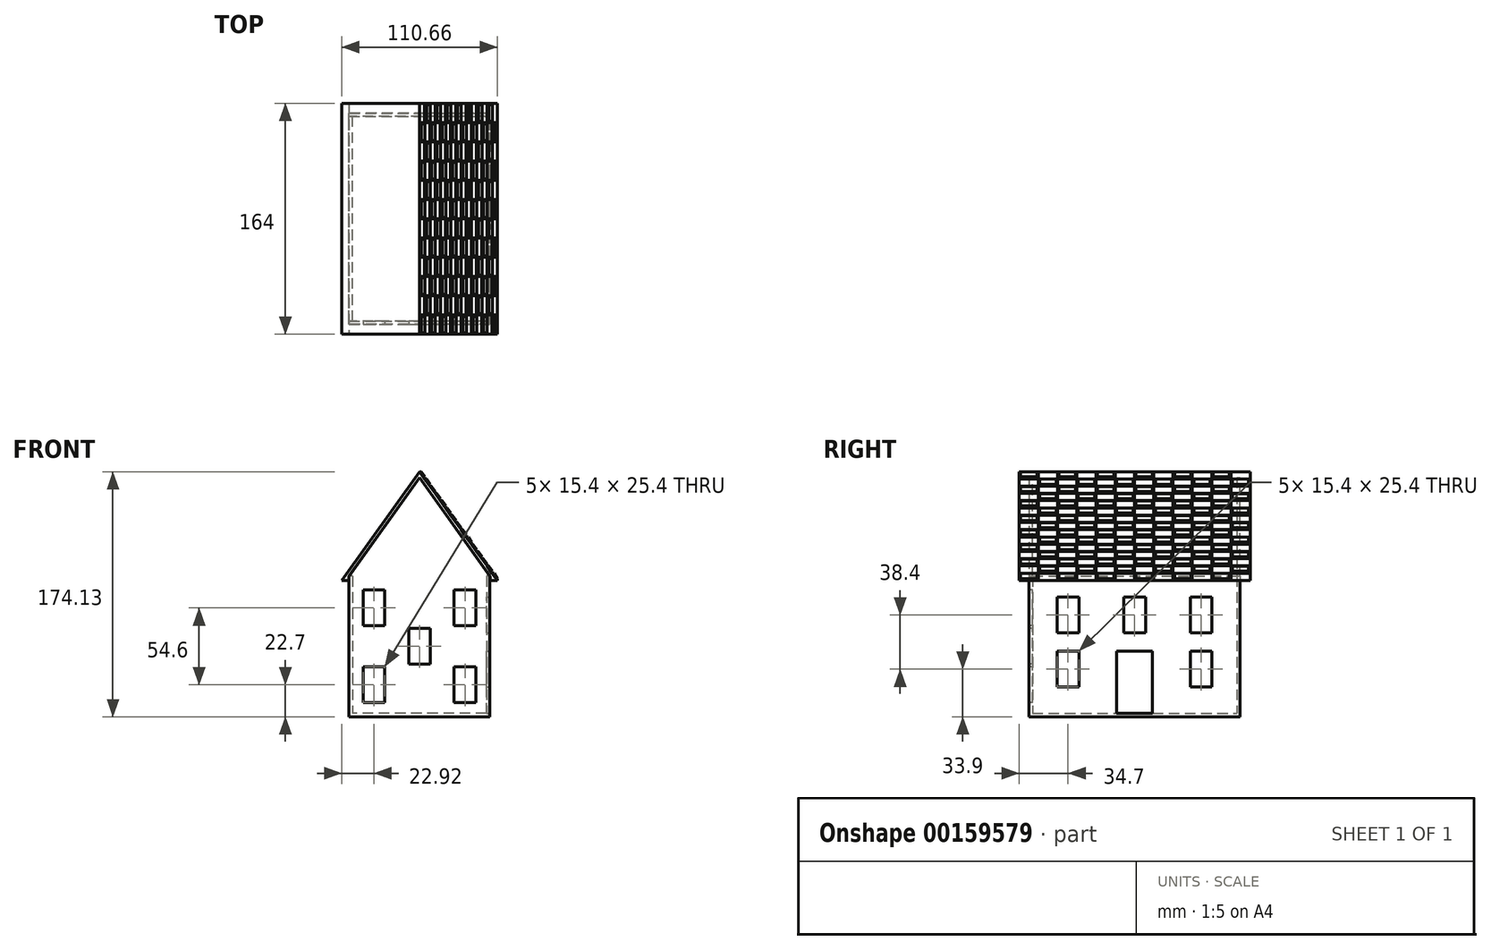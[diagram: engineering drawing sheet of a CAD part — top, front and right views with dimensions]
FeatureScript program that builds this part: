
annotation { "Feature Type Name" : "Feature", "Feature Type Description" : "" }
export const myFeature = defineFeature(function(context is Context, id is Id, definition is map)
    precondition{}
    {
        {
            assignVariable(context, id + "F0", {"name" : "T", "anyValue" : 2.4 * mm});
        }
        {
            var Q0;
            Q0=qCreatedBy(makeId("Top.planeOp"),FACE);
            var sketch = newSketch(context, id + "F1", { "sketchPlane" : qUnion([Q0])});
            skLineSegment(sketch, "E0.bottom", {"start": v(50, -75) * mm, "end": v(-50, -75) * mm});
            skLineSegment(sketch, "E0.top", {"start": v(50, 75) * mm, "end": v(-50, 75) * mm});
            skLineSegment(sketch, "E0.left", {"start": v(50, -75) * mm, "end": v(50, 75) * mm});
            skLineSegment(sketch, "E0.right", {"start": v(-50, -75) * mm, "end": v(-50, 75) * mm});
            skPoint(sketch, "E0.middle", {"position": v(0, 0) * mm});
            skSolve(sketch);
        }
        {
            var Q0;
            Q0=makeQuery(id+"F1.imprint","IMPRINT",FACE,{"disambiguationData":[TD([[makeQuery(id+"F1.imprint","IMPRINT",EDGE,{"derivedFrom":sQuery(id+"F1.wireOp",EDGE,"E0.bottom")}),-1.0]])]});
            extrude(context, id + "F2", {"entities" : qUnion([Q0]), "depth" : 100 * mm});
        }
        {
            var Q0;
            Q0=makeQuery(id+"F2.opExtrude","CAP_FACE",FACE,{"disambiguationData":[OSD([sQuery(id+"F1.wireOp",EDGE,"E0.bottom"),sQuery(id+"F1.wireOp",EDGE,"E0.top"),sQuery(id+"F1.wireOp",EDGE,"E0.left"),sQuery(id+"F1.wireOp",EDGE,"E0.right")])],"isStart":false});
            shell(context, id + "F3", {"entities" : qUnion([Q0]), "thickness" : getVariable(context, 'T')});
        }
        {
            var Q0;
            Q0=makeQuery(id+"F2.opExtrude","SWEPT_FACE",FACE,{"disambiguationData":[OSD([sQuery(id+"F1.wireOp",EDGE,"E0.bottom")])]});
            var sketch = newSketch(context, id + "F4", { "sketchPlane" : qUnion([Q0])});
            skLineSegment(sketch, "E1", {"start": v(-50, 100) * mm, "end": v(0, 170) * mm});
            skLineSegment(sketch, "E2", {"start": v(0, 170) * mm, "end": v(50, 100) * mm});
            skLineSegment(sketch, "E3", {"start": v(-50, 100) * mm, "end": v(50, 100) * mm});
            skSolve(sketch);
        }
        {
            var Q0;
            Q0=qSketchRegion(id+"F4",true);
            extrude(context, id + "F5", {"entities" : qUnion([Q0]), "operationType" : NewBodyOperationType.ADD, "oppositeDirection" : true, "depth" : getVariable(context, 'T')});
        }
        {
            var Q0;
            Q0=makeQuery(id+"F2.opExtrude","SWEPT_FACE",FACE,{"disambiguationData":[OSD([sQuery(id+"F1.wireOp",EDGE,"E0.top")])]});
            var sketch = newSketch(context, id + "F6", { "sketchPlane" : qUnion([Q0])});
            skLineSegment(sketch, "E4.0", {"start": v(50, 100) * mm, "end": v(-50, 100) * mm});
            skLineSegment(sketch, "E5.0", {"start": v(0, 170) * mm, "end": v(-50, 100) * mm});
            skLineSegment(sketch, "E6.0", {"start": v(50, 100) * mm, "end": v(0, 170) * mm});
            skSolve(sketch);
        }
        {
            var Q0;
            Q0=qSketchRegion(id+"F6",true);
            extrude(context, id + "F7", {"entities" : qUnion([Q0]), "operationType" : NewBodyOperationType.ADD, "oppositeDirection" : true, "depth" : getVariable(context, 'T')});
        }
        {
            var Q0;
            Q0=makeQuery(id+"F5.boolean.opBoolean","MERGE",FACE,{"derivedFrom":[makeQuery(id+"F2.opExtrude","SWEPT_FACE",FACE,{"disambiguationData":[OSD([sQuery(id+"F1.wireOp",EDGE,"E0.bottom")])]}),makeQuery(id+"F5.opExtrude","CAP_FACE",FACE,{"disambiguationData":[OSD([sQuery(id+"F4.wireOp",EDGE,"E1"),sQuery(id+"F4.wireOp",EDGE,"E2"),sQuery(id+"F4.wireOp",EDGE,"E3")])],"isStart":true})]});
            var sketch = newSketch(context, id + "F8", { "sketchPlane" : qUnion([Q0])});
            skLineSegment(sketch, "E7.bottom", {"start": v(-40, 90) * mm, "end": v(-24.6, 90) * mm});
            skLineSegment(sketch, "E7.top", {"start": v(-40, 64.6) * mm, "end": v(-24.6, 64.6) * mm});
            skLineSegment(sketch, "E7.left", {"start": v(-40, 90) * mm, "end": v(-40, 64.6) * mm});
            skLineSegment(sketch, "E7.right", {"start": v(-24.6, 90) * mm, "end": v(-24.6, 64.6) * mm});
            skLineSegment(sketch, "E8.bottom", {"start": v(24.6, 90) * mm, "end": v(40, 90) * mm});
            skLineSegment(sketch, "E8.top", {"start": v(24.6, 64.6) * mm, "end": v(40, 64.6) * mm});
            skLineSegment(sketch, "E8.left", {"start": v(24.6, 90) * mm, "end": v(24.6, 64.6) * mm});
            skLineSegment(sketch, "E8.right", {"start": v(40, 90) * mm, "end": v(40, 64.6) * mm});
            skPoint(sketch, "E9", {"position": v(0, 50) * mm});
            skLineSegment(sketch, "E10.bottom", {"start": v(-7.7, 62.7) * mm, "end": v(7.7, 62.7) * mm});
            skLineSegment(sketch, "E10.top", {"start": v(-7.7, 37.3) * mm, "end": v(7.7, 37.3) * mm});
            skLineSegment(sketch, "E10.left", {"start": v(-7.7, 62.7) * mm, "end": v(-7.7, 37.3) * mm});
            skLineSegment(sketch, "E10.right", {"start": v(7.7, 62.7) * mm, "end": v(7.7, 37.3) * mm});
            skLineSegment(sketch, "E11.bottom", {"start": v(-40, 35.4) * mm, "end": v(-24.6, 35.4) * mm});
            skLineSegment(sketch, "E11.top", {"start": v(-40, 10) * mm, "end": v(-24.6, 10) * mm});
            skLineSegment(sketch, "E11.left", {"start": v(-40, 35.4) * mm, "end": v(-40, 10) * mm});
            skLineSegment(sketch, "E11.right", {"start": v(-24.6, 35.4) * mm, "end": v(-24.6, 10) * mm});
            skLineSegment(sketch, "E12.bottom", {"start": v(24.6, 35.4) * mm, "end": v(40, 35.4) * mm});
            skLineSegment(sketch, "E12.top", {"start": v(24.6, 10) * mm, "end": v(40, 10) * mm});
            skLineSegment(sketch, "E12.left", {"start": v(24.6, 35.4) * mm, "end": v(24.6, 10) * mm});
            skLineSegment(sketch, "E12.right", {"start": v(40, 35.4) * mm, "end": v(40, 10) * mm});
            skPoint(sketch, "E13.positionSnap0", {"position": v(0, 62.7) * mm});
            skLineSegment(sketch, "E14", {"start": v(-66.45, 100) * mm, "end": v(66.45, 100) * mm, "construction": true});
            skLineSegment(sketch, "E15", {"start": v(-66.45, 90) * mm, "end": v(66.45, 90) * mm, "construction": true});
            skLineSegment(sketch, "E16", {"start": v(-66.45, 0) * mm, "end": v(66.45, 0) * mm, "construction": true});
            skLineSegment(sketch, "E17", {"start": v(-50, 110.2) * mm, "end": v(-50, -10.46) * mm, "construction": true});
            skLineSegment(sketch, "E18", {"start": v(-40, 110.2) * mm, "end": v(-40, -10.46) * mm, "construction": true});
            skLineSegment(sketch, "E19", {"start": v(50, 110.2) * mm, "end": v(50, -10.46) * mm, "construction": true});
            skLineSegment(sketch, "E20", {"start": v(40, 110.2) * mm, "end": v(40, -10.46) * mm, "construction": true});
            skPoint(sketch, "E21", {"position": v(-40, 49.87) * mm});
            skPoint(sketch, "E22", {"position": v(-50, 50) * mm});
            skPoint(sketch, "E23", {"position": v(0, 90) * mm});
            skLineSegment(sketch, "E24", {"start": v(66.45, 10) * mm, "end": v(-66.45, 10) * mm, "construction": true});
            skSolve(sketch);
        }
        {
            var Q0;
            Q0=makeQuery(id+"F8.imprint","IMPRINT",FACE,{"disambiguationData":[TD([[makeQuery(id+"F8.imprint","IMPRINT",EDGE,{"derivedFrom":sQuery(id+"F8.wireOp",EDGE,"E7.bottom")}),-1.0]])]});
            var Q1;
            Q1=makeQuery(id+"F8.imprint","IMPRINT",FACE,{"disambiguationData":[TD([[makeQuery(id+"F8.imprint","IMPRINT",EDGE,{"derivedFrom":sQuery(id+"F8.wireOp",EDGE,"E8.bottom")}),-1.0]])]});
            var Q2;
            Q2=makeQuery(id+"F8.imprint","IMPRINT",FACE,{"disambiguationData":[TD([[makeQuery(id+"F8.imprint","IMPRINT",EDGE,{"derivedFrom":sQuery(id+"F8.wireOp",EDGE,"E10.bottom")}),-1.0]])]});
            var Q3;
            Q3=makeQuery(id+"F8.imprint","IMPRINT",FACE,{"disambiguationData":[TD([[makeQuery(id+"F8.imprint","IMPRINT",EDGE,{"derivedFrom":sQuery(id+"F8.wireOp",EDGE,"E12.bottom")}),-1.0]])]});
            var Q4;
            Q4=makeQuery(id+"F8.imprint","IMPRINT",FACE,{"disambiguationData":[TD([[makeQuery(id+"F8.imprint","IMPRINT",EDGE,{"derivedFrom":sQuery(id+"F8.wireOp",EDGE,"E11.bottom")}),-1.0]])]});
            extrude(context, id + "F9", {"entities" : qUnion([Q0, Q1, Q2, Q3, Q4]), "operationType" : NewBodyOperationType.REMOVE, "endBound" : BoundingType.UP_TO_NEXT, "oppositeDirection" : true, "depth" : 25 * mm});
        }
        {
            var Q0;
            Q0=makeQuery(id+"F2.opExtrude","SWEPT_FACE",FACE,{"disambiguationData":[OSD([sQuery(id+"F1.wireOp",EDGE,"E0.left")])]});
            var sketch = newSketch(context, id + "F10", { "sketchPlane" : qUnion([Q0])});
            skLineSegment(sketch, "E25.bottom", {"start": v(-39.6, 59.6) * mm, "end": v(-55, 59.6) * mm});
            skLineSegment(sketch, "E25.top", {"start": v(-39.6, 85) * mm, "end": v(-55, 85) * mm});
            skLineSegment(sketch, "E25.left", {"start": v(-39.6, 59.6) * mm, "end": v(-39.6, 85) * mm});
            skLineSegment(sketch, "E25.right", {"start": v(-55, 59.6) * mm, "end": v(-55, 85) * mm});
            skPoint(sketch, "E25.middle", {"position": v(-47.3, 72.3) * mm});
            skLineSegment(sketch, "E26.bottom", {"start": v(55, 59.6) * mm, "end": v(39.6, 59.6) * mm});
            skLineSegment(sketch, "E26.top", {"start": v(55, 85) * mm, "end": v(39.6, 85) * mm});
            skLineSegment(sketch, "E26.left", {"start": v(55, 59.6) * mm, "end": v(55, 85) * mm});
            skLineSegment(sketch, "E26.right", {"start": v(39.6, 59.6) * mm, "end": v(39.6, 85) * mm});
            skPoint(sketch, "E26.middle", {"position": v(47.3, 72.3) * mm});
            skLineSegment(sketch, "E27.bottom", {"start": v(-39.6, 21.2) * mm, "end": v(-55, 21.2) * mm});
            skLineSegment(sketch, "E27.top", {"start": v(-39.6, 46.6) * mm, "end": v(-55, 46.6) * mm});
            skLineSegment(sketch, "E27.left", {"start": v(-39.6, 21.2) * mm, "end": v(-39.6, 46.6) * mm});
            skLineSegment(sketch, "E27.right", {"start": v(-55, 21.2) * mm, "end": v(-55, 46.6) * mm});
            skPoint(sketch, "E27.middle", {"position": v(-47.3, 33.9) * mm});
            skLineSegment(sketch, "E28.bottom", {"start": v(55, 21.2) * mm, "end": v(39.6, 21.2) * mm});
            skLineSegment(sketch, "E28.top", {"start": v(55, 46.6) * mm, "end": v(39.6, 46.6) * mm});
            skLineSegment(sketch, "E28.left", {"start": v(55, 21.2) * mm, "end": v(55, 46.6) * mm});
            skLineSegment(sketch, "E28.right", {"start": v(39.6, 21.2) * mm, "end": v(39.6, 46.6) * mm});
            skPoint(sketch, "E28.middle", {"position": v(47.3, 33.9) * mm});
            skLineSegment(sketch, "E29.bottom", {"start": v(7.7, 59.6) * mm, "end": v(-7.7, 59.6) * mm});
            skLineSegment(sketch, "E29.top", {"start": v(7.7, 85) * mm, "end": v(-7.7, 85) * mm});
            skLineSegment(sketch, "E29.left", {"start": v(7.7, 59.6) * mm, "end": v(7.7, 85) * mm});
            skLineSegment(sketch, "E29.right", {"start": v(-7.7, 59.6) * mm, "end": v(-7.7, 85) * mm});
            skPoint(sketch, "E29.middle", {"position": v(0, 72.3) * mm});
            skLineSegment(sketch, "E30", {"start": v(-82.85, 2.4) * mm, "end": v(78.68, 2.4) * mm, "construction": true});
            skLineSegment(sketch, "E31.bottom", {"start": v(-12.7, 2.4) * mm, "end": v(12.7, 2.4) * mm});
            skLineSegment(sketch, "E31.top", {"start": v(-12.7, 46.6) * mm, "end": v(12.7, 46.6) * mm});
            skLineSegment(sketch, "E31.left", {"start": v(-12.7, 2.4) * mm, "end": v(-12.7, 46.6) * mm});
            skLineSegment(sketch, "E31.right", {"start": v(12.7, 2.4) * mm, "end": v(12.7, 46.6) * mm});
            skPoint(sketch, "E32", {"position": v(0, 46.6) * mm});
            skSolve(sketch);
        }
        {
            var Q0;
            Q0=qSketchRegion(id+"F10",true);
            extrude(context, id + "F11", {"entities" : qUnion([Q0]), "operationType" : NewBodyOperationType.REMOVE, "endBound" : BoundingType.UP_TO_NEXT, "oppositeDirection" : true, "depth" : 25 * mm});
        }
        {
            var Q0;
            Q0=makeQuery(id+"F5.boolean.opBoolean","MERGE",FACE,{"derivedFrom":[makeQuery(id+"F2.opExtrude","SWEPT_FACE",FACE,{"disambiguationData":[OSD([sQuery(id+"F1.wireOp",EDGE,"E0.bottom")])]}),makeQuery(id+"F5.opExtrude","CAP_FACE",FACE,{"disambiguationData":[OSD([sQuery(id+"F4.wireOp",EDGE,"E1"),sQuery(id+"F4.wireOp",EDGE,"E2"),sQuery(id+"F4.wireOp",EDGE,"E3")])],"isStart":true})]});
            cPlane(context, id + "F12", {"entities" : qUnion([Q0]), "cplaneType" : CPlaneType.OFFSET, "offset" : 7 * mm, "width" : 150 * mm, "height" : 150 * mm});
        }
        {
            var Q0;
            Q0=makeQuery(id+"F7.boolean.opBoolean","MERGE",FACE,{"derivedFrom":[makeQuery(id+"F2.opExtrude","SWEPT_FACE",FACE,{"disambiguationData":[OSD([sQuery(id+"F1.wireOp",EDGE,"E0.top")])]}),makeQuery(id+"F7.opExtrude","CAP_FACE",FACE,{"disambiguationData":[OSD([sQuery(id+"F6.wireOp",EDGE,"E4.0"),sQuery(id+"F6.wireOp",EDGE,"E5.0"),sQuery(id+"F6.wireOp",EDGE,"E6.0")])],"isStart":true})]});
            cPlane(context, id + "F13", {"entities" : qUnion([Q0]), "cplaneType" : CPlaneType.OFFSET, "offset" : 7 * mm, "width" : 150 * mm, "height" : 150 * mm});
        }
        {
            var Q0;
            Q0=qCreatedBy(id+"F12.planeOp",FACE);
            var sketch = newSketch(context, id + "F14", { "sketchPlane" : qUnion([Q0])});
            skPoint(sketch, "E33", {"position": v(0, 170) * mm});
            skPoint(sketch, "E34", {"position": v(50, 100) * mm});
            skPoint(sketch, "E35", {"position": v(-50, 100) * mm});
            skLineSegment(sketch, "E36", {"start": v(-55.22, 96.82) * mm, "end": v(0, 174.13) * mm});
            skLineSegment(sketch, "E37", {"start": v(-55.22, 96.82) * mm, "end": v(-50.2, 96.82) * mm});
            skLineSegment(sketch, "E38", {"start": v(0, 170) * mm, "end": v(-50, 100) * mm});
            skLineSegment(sketch, "E39", {"start": v(-50, 100) * mm, "end": v(-50.2, 99.72) * mm});
            skLineSegment(sketch, "E40", {"start": v(-50.2, 99.72) * mm, "end": v(-50.2, 96.82) * mm});
            skLineSegment(sketch, "E41", {"start": v(0, 181.99) * mm, "end": v(0, -15.78) * mm, "construction": true});
            skLineSegment(sketch, "E42.MirrorCS", {"start": v(0, 170) * mm, "end": v(50, 100) * mm});
            skLineSegment(sketch, "E43.MirrorCS", {"start": v(50, 100) * mm, "end": v(50.2, 99.72) * mm});
            skLineSegment(sketch, "E44.MirrorCS", {"start": v(50.2, 99.72) * mm, "end": v(50.2, 96.82) * mm});
            skLineSegment(sketch, "E45.MirrorCS", {"start": v(55.22, 96.82) * mm, "end": v(0, 174.13) * mm});
            skLineSegment(sketch, "E46.MirrorCS", {"start": v(55.22, 96.82) * mm, "end": v(50.2, 96.82) * mm});
            skSolve(sketch);
        }
        {
            var Q0;
            Q0=qSketchRegion(id+"F14",true);
            var Q1;
            Q1=qCreatedBy(id+"F13.planeOp",FACE);
            extrude(context, id + "F15", {"entities" : qUnion([Q0]), "oppositeDirection" : true, "endBoundEntityFace" : qUnion([Q1]), "depth" : 164 * mm});
        }
        {
            var Q0;
            Q0=makeQuery(id+"F15.opExtrude","SWEPT_FACE",FACE,{"disambiguationData":[OSD([sQuery(id+"F14.wireOp",EDGE,"E45.MirrorCS")])]});
            var sketch = newSketch(context, id + "F16", { "sketchPlane" : qUnion([Q0])});
            skLineSegment(sketch, "E47", {"start": v(-82, 141.7) * mm, "end": v(-68.33, 141.7) * mm});
            skLineSegment(sketch, "E48", {"start": v(-68.33, 141.7) * mm, "end": v(-68.33, 135.36) * mm});
            skLineSegment(sketch, "E49", {"start": v(-68.33, 135.36) * mm, "end": v(-82, 135.36) * mm});
            skLineSegment(sketch, "E50", {"start": v(-82, 135.36) * mm, "end": v(-82, 141.7) * mm});
            skLineSegment(sketch, "E51.0.1.0", {"start": v(-82, 129.03) * mm, "end": v(-68.33, 129.03) * mm});
            skLineSegment(sketch, "E51.0.1.1", {"start": v(-82, 122.7) * mm, "end": v(-82, 129.03) * mm});
            skLineSegment(sketch, "E51.0.1.2", {"start": v(-68.33, 129.03) * mm, "end": v(-68.33, 122.7) * mm});
            skLineSegment(sketch, "E51.0.1.3", {"start": v(-68.33, 122.7) * mm, "end": v(-82, 122.7) * mm});
            skLineSegment(sketch, "E51.0.2.0", {"start": v(-82, 116.37) * mm, "end": v(-68.33, 116.37) * mm});
            skLineSegment(sketch, "E51.0.2.1", {"start": v(-82, 110.03) * mm, "end": v(-82, 116.37) * mm});
            skLineSegment(sketch, "E51.0.2.2", {"start": v(-68.33, 116.37) * mm, "end": v(-68.33, 110.03) * mm});
            skLineSegment(sketch, "E51.0.2.3", {"start": v(-68.33, 110.03) * mm, "end": v(-82, 110.03) * mm});
            skLineSegment(sketch, "E51.0.3.0", {"start": v(-82, 103.7) * mm, "end": v(-68.33, 103.7) * mm});
            skLineSegment(sketch, "E51.0.3.1", {"start": v(-82, 97.37) * mm, "end": v(-82, 103.7) * mm});
            skLineSegment(sketch, "E51.0.3.2", {"start": v(-68.33, 103.7) * mm, "end": v(-68.33, 97.37) * mm});
            skLineSegment(sketch, "E51.0.3.3", {"start": v(-68.33, 97.37) * mm, "end": v(-82, 97.37) * mm});
            skLineSegment(sketch, "E51.0.4.0", {"start": v(-82, 91.04) * mm, "end": v(-68.33, 91.04) * mm});
            skLineSegment(sketch, "E51.0.4.1", {"start": v(-82, 84.7) * mm, "end": v(-82, 91.04) * mm});
            skLineSegment(sketch, "E51.0.4.2", {"start": v(-68.33, 91.04) * mm, "end": v(-68.33, 84.7) * mm});
            skLineSegment(sketch, "E51.0.4.3", {"start": v(-68.33, 84.7) * mm, "end": v(-82, 84.7) * mm});
            skLineSegment(sketch, "E51.0.5.0", {"start": v(-82, 78.38) * mm, "end": v(-68.33, 78.38) * mm});
            skLineSegment(sketch, "E51.0.5.1", {"start": v(-82, 72.04) * mm, "end": v(-82, 78.38) * mm});
            skLineSegment(sketch, "E51.0.5.2", {"start": v(-68.33, 78.38) * mm, "end": v(-68.33, 72.04) * mm});
            skLineSegment(sketch, "E51.0.5.3", {"start": v(-68.33, 72.04) * mm, "end": v(-82, 72.04) * mm});
            skLineSegment(sketch, "E51.0.6.0", {"start": v(-82, 65.71) * mm, "end": v(-68.33, 65.71) * mm});
            skLineSegment(sketch, "E51.0.6.1", {"start": v(-82, 59.38) * mm, "end": v(-82, 65.71) * mm});
            skLineSegment(sketch, "E51.0.6.2", {"start": v(-68.33, 65.71) * mm, "end": v(-68.33, 59.38) * mm});
            skLineSegment(sketch, "E51.0.6.3", {"start": v(-68.33, 59.38) * mm, "end": v(-82, 59.38) * mm});
            skLineSegment(sketch, "E51.0.7.0", {"start": v(-82, 53.05) * mm, "end": v(-68.33, 53.05) * mm});
            skLineSegment(sketch, "E51.0.7.1", {"start": v(-82, 46.72) * mm, "end": v(-82, 53.05) * mm});
            skLineSegment(sketch, "E51.0.7.2", {"start": v(-68.33, 53.05) * mm, "end": v(-68.33, 46.72) * mm});
            skLineSegment(sketch, "E51.0.7.3", {"start": v(-68.33, 46.72) * mm, "end": v(-82, 46.72) * mm});
            skLineSegment(sketch, "E51.1.0.0", {"start": v(-54.67, 141.7) * mm, "end": v(-41, 141.7) * mm});
            skLineSegment(sketch, "E51.1.0.1", {"start": v(-54.67, 135.36) * mm, "end": v(-54.67, 141.7) * mm});
            skLineSegment(sketch, "E51.1.0.2", {"start": v(-41, 141.7) * mm, "end": v(-41, 135.36) * mm});
            skLineSegment(sketch, "E51.1.0.3", {"start": v(-41, 135.36) * mm, "end": v(-54.67, 135.36) * mm});
            skLineSegment(sketch, "E51.1.1.0", {"start": v(-54.67, 129.03) * mm, "end": v(-41, 129.03) * mm});
            skLineSegment(sketch, "E51.1.1.1", {"start": v(-54.67, 122.7) * mm, "end": v(-54.67, 129.03) * mm});
            skLineSegment(sketch, "E51.1.1.2", {"start": v(-41, 129.03) * mm, "end": v(-41, 122.7) * mm});
            skLineSegment(sketch, "E51.1.1.3", {"start": v(-41, 122.7) * mm, "end": v(-54.67, 122.7) * mm});
            skLineSegment(sketch, "E51.1.2.0", {"start": v(-54.67, 116.37) * mm, "end": v(-41, 116.37) * mm});
            skLineSegment(sketch, "E51.1.2.1", {"start": v(-54.67, 110.03) * mm, "end": v(-54.67, 116.37) * mm});
            skLineSegment(sketch, "E51.1.2.2", {"start": v(-41, 116.37) * mm, "end": v(-41, 110.03) * mm});
            skLineSegment(sketch, "E51.1.2.3", {"start": v(-41, 110.03) * mm, "end": v(-54.67, 110.03) * mm});
            skLineSegment(sketch, "E51.1.3.0", {"start": v(-54.67, 103.7) * mm, "end": v(-41, 103.7) * mm});
            skLineSegment(sketch, "E51.1.3.1", {"start": v(-54.67, 97.37) * mm, "end": v(-54.67, 103.7) * mm});
            skLineSegment(sketch, "E51.1.3.2", {"start": v(-41, 103.7) * mm, "end": v(-41, 97.37) * mm});
            skLineSegment(sketch, "E51.1.3.3", {"start": v(-41, 97.37) * mm, "end": v(-54.67, 97.37) * mm});
            skLineSegment(sketch, "E51.1.4.0", {"start": v(-54.67, 91.04) * mm, "end": v(-41, 91.04) * mm});
            skLineSegment(sketch, "E51.1.4.1", {"start": v(-54.67, 84.7) * mm, "end": v(-54.67, 91.04) * mm});
            skLineSegment(sketch, "E51.1.4.2", {"start": v(-41, 91.04) * mm, "end": v(-41, 84.7) * mm});
            skLineSegment(sketch, "E51.1.4.3", {"start": v(-41, 84.7) * mm, "end": v(-54.67, 84.7) * mm});
            skLineSegment(sketch, "E51.1.5.0", {"start": v(-54.67, 78.38) * mm, "end": v(-41, 78.38) * mm});
            skLineSegment(sketch, "E51.1.5.1", {"start": v(-54.67, 72.04) * mm, "end": v(-54.67, 78.38) * mm});
            skLineSegment(sketch, "E51.1.5.2", {"start": v(-41, 78.38) * mm, "end": v(-41, 72.04) * mm});
            skLineSegment(sketch, "E51.1.5.3", {"start": v(-41, 72.04) * mm, "end": v(-54.67, 72.04) * mm});
            skLineSegment(sketch, "E51.1.6.0", {"start": v(-54.67, 65.71) * mm, "end": v(-41, 65.71) * mm});
            skLineSegment(sketch, "E51.1.6.1", {"start": v(-54.67, 59.38) * mm, "end": v(-54.67, 65.71) * mm});
            skLineSegment(sketch, "E51.1.6.2", {"start": v(-41, 65.71) * mm, "end": v(-41, 59.38) * mm});
            skLineSegment(sketch, "E51.1.6.3", {"start": v(-41, 59.38) * mm, "end": v(-54.67, 59.38) * mm});
            skLineSegment(sketch, "E51.1.7.0", {"start": v(-54.67, 53.05) * mm, "end": v(-41, 53.05) * mm});
            skLineSegment(sketch, "E51.1.7.1", {"start": v(-54.67, 46.72) * mm, "end": v(-54.67, 53.05) * mm});
            skLineSegment(sketch, "E51.1.7.2", {"start": v(-41, 53.05) * mm, "end": v(-41, 46.72) * mm});
            skLineSegment(sketch, "E51.1.7.3", {"start": v(-41, 46.72) * mm, "end": v(-54.67, 46.72) * mm});
            skLineSegment(sketch, "E51.2.0.0", {"start": v(-27.33, 141.7) * mm, "end": v(-13.67, 141.7) * mm});
            skLineSegment(sketch, "E51.2.0.1", {"start": v(-27.33, 135.36) * mm, "end": v(-27.33, 141.7) * mm});
            skLineSegment(sketch, "E51.2.0.2", {"start": v(-13.67, 141.7) * mm, "end": v(-13.67, 135.36) * mm});
            skLineSegment(sketch, "E51.2.0.3", {"start": v(-13.67, 135.36) * mm, "end": v(-27.33, 135.36) * mm});
            skLineSegment(sketch, "E51.2.1.0", {"start": v(-27.33, 129.03) * mm, "end": v(-13.67, 129.03) * mm});
            skLineSegment(sketch, "E51.2.1.1", {"start": v(-27.33, 122.7) * mm, "end": v(-27.33, 129.03) * mm});
            skLineSegment(sketch, "E51.2.1.2", {"start": v(-13.67, 129.03) * mm, "end": v(-13.67, 122.7) * mm});
            skLineSegment(sketch, "E51.2.1.3", {"start": v(-13.67, 122.7) * mm, "end": v(-27.33, 122.7) * mm});
            skLineSegment(sketch, "E51.2.2.0", {"start": v(-27.33, 116.37) * mm, "end": v(-13.67, 116.37) * mm});
            skLineSegment(sketch, "E51.2.2.1", {"start": v(-27.33, 110.03) * mm, "end": v(-27.33, 116.37) * mm});
            skLineSegment(sketch, "E51.2.2.2", {"start": v(-13.67, 116.37) * mm, "end": v(-13.67, 110.03) * mm});
            skLineSegment(sketch, "E51.2.2.3", {"start": v(-13.67, 110.03) * mm, "end": v(-27.33, 110.03) * mm});
            skLineSegment(sketch, "E51.2.3.0", {"start": v(-27.33, 103.7) * mm, "end": v(-13.67, 103.7) * mm});
            skLineSegment(sketch, "E51.2.3.1", {"start": v(-27.33, 97.37) * mm, "end": v(-27.33, 103.7) * mm});
            skLineSegment(sketch, "E51.2.3.2", {"start": v(-13.67, 103.7) * mm, "end": v(-13.67, 97.37) * mm});
            skLineSegment(sketch, "E51.2.3.3", {"start": v(-13.67, 97.37) * mm, "end": v(-27.33, 97.37) * mm});
            skLineSegment(sketch, "E51.2.4.0", {"start": v(-27.33, 91.04) * mm, "end": v(-13.67, 91.04) * mm});
            skLineSegment(sketch, "E51.2.4.1", {"start": v(-27.33, 84.7) * mm, "end": v(-27.33, 91.04) * mm});
            skLineSegment(sketch, "E51.2.4.2", {"start": v(-13.67, 91.04) * mm, "end": v(-13.67, 84.7) * mm});
            skLineSegment(sketch, "E51.2.4.3", {"start": v(-13.67, 84.7) * mm, "end": v(-27.33, 84.7) * mm});
            skLineSegment(sketch, "E51.2.5.0", {"start": v(-27.33, 78.38) * mm, "end": v(-13.67, 78.38) * mm});
            skLineSegment(sketch, "E51.2.5.1", {"start": v(-27.33, 72.04) * mm, "end": v(-27.33, 78.38) * mm});
            skLineSegment(sketch, "E51.2.5.2", {"start": v(-13.67, 78.38) * mm, "end": v(-13.67, 72.04) * mm});
            skLineSegment(sketch, "E51.2.5.3", {"start": v(-13.67, 72.04) * mm, "end": v(-27.33, 72.04) * mm});
            skLineSegment(sketch, "E51.2.6.0", {"start": v(-27.33, 65.71) * mm, "end": v(-13.67, 65.71) * mm});
            skLineSegment(sketch, "E51.2.6.1", {"start": v(-27.33, 59.38) * mm, "end": v(-27.33, 65.71) * mm});
            skLineSegment(sketch, "E51.2.6.2", {"start": v(-13.67, 65.71) * mm, "end": v(-13.67, 59.38) * mm});
            skLineSegment(sketch, "E51.2.6.3", {"start": v(-13.67, 59.38) * mm, "end": v(-27.33, 59.38) * mm});
            skLineSegment(sketch, "E51.2.7.0", {"start": v(-27.33, 53.05) * mm, "end": v(-13.67, 53.05) * mm});
            skLineSegment(sketch, "E51.2.7.1", {"start": v(-27.33, 46.72) * mm, "end": v(-27.33, 53.05) * mm});
            skLineSegment(sketch, "E51.2.7.2", {"start": v(-13.67, 53.05) * mm, "end": v(-13.67, 46.72) * mm});
            skLineSegment(sketch, "E51.2.7.3", {"start": v(-13.67, 46.72) * mm, "end": v(-27.33, 46.72) * mm});
            skLineSegment(sketch, "E51.3.0.0", {"start": v(0, 141.7) * mm, "end": v(13.67, 141.7) * mm});
            skLineSegment(sketch, "E51.3.0.1", {"start": v(0, 135.36) * mm, "end": v(0, 141.7) * mm});
            skLineSegment(sketch, "E51.3.0.2", {"start": v(13.67, 141.7) * mm, "end": v(13.67, 135.36) * mm});
            skLineSegment(sketch, "E51.3.0.3", {"start": v(13.67, 135.36) * mm, "end": v(0, 135.36) * mm});
            skLineSegment(sketch, "E51.3.1.0", {"start": v(0, 129.03) * mm, "end": v(13.67, 129.03) * mm});
            skLineSegment(sketch, "E51.3.1.1", {"start": v(0, 122.7) * mm, "end": v(0, 129.03) * mm});
            skLineSegment(sketch, "E51.3.1.2", {"start": v(13.67, 129.03) * mm, "end": v(13.67, 122.7) * mm});
            skLineSegment(sketch, "E51.3.1.3", {"start": v(13.67, 122.7) * mm, "end": v(0, 122.7) * mm});
            skLineSegment(sketch, "E51.3.2.0", {"start": v(0, 116.37) * mm, "end": v(13.67, 116.37) * mm});
            skLineSegment(sketch, "E51.3.2.1", {"start": v(0, 110.03) * mm, "end": v(0, 116.37) * mm});
            skLineSegment(sketch, "E51.3.2.2", {"start": v(13.67, 116.37) * mm, "end": v(13.67, 110.03) * mm});
            skLineSegment(sketch, "E51.3.2.3", {"start": v(13.67, 110.03) * mm, "end": v(0, 110.03) * mm});
            skLineSegment(sketch, "E51.3.3.0", {"start": v(0, 103.7) * mm, "end": v(13.67, 103.7) * mm});
            skLineSegment(sketch, "E51.3.3.1", {"start": v(0, 97.37) * mm, "end": v(0, 103.7) * mm});
            skLineSegment(sketch, "E51.3.3.2", {"start": v(13.67, 103.7) * mm, "end": v(13.67, 97.37) * mm});
            skLineSegment(sketch, "E51.3.3.3", {"start": v(13.67, 97.37) * mm, "end": v(0, 97.37) * mm});
            skLineSegment(sketch, "E51.3.4.0", {"start": v(0, 91.04) * mm, "end": v(13.67, 91.04) * mm});
            skLineSegment(sketch, "E51.3.4.1", {"start": v(0, 84.7) * mm, "end": v(0, 91.04) * mm});
            skLineSegment(sketch, "E51.3.4.2", {"start": v(13.67, 91.04) * mm, "end": v(13.67, 84.7) * mm});
            skLineSegment(sketch, "E51.3.4.3", {"start": v(13.67, 84.7) * mm, "end": v(0, 84.7) * mm});
            skLineSegment(sketch, "E51.3.5.0", {"start": v(0, 78.38) * mm, "end": v(13.67, 78.38) * mm});
            skLineSegment(sketch, "E51.3.5.1", {"start": v(0, 72.04) * mm, "end": v(0, 78.38) * mm});
            skLineSegment(sketch, "E51.3.5.2", {"start": v(13.67, 78.38) * mm, "end": v(13.67, 72.04) * mm});
            skLineSegment(sketch, "E51.3.5.3", {"start": v(13.67, 72.04) * mm, "end": v(0, 72.04) * mm});
            skLineSegment(sketch, "E51.3.6.0", {"start": v(0, 65.71) * mm, "end": v(13.67, 65.71) * mm});
            skLineSegment(sketch, "E51.3.6.1", {"start": v(0, 59.38) * mm, "end": v(0, 65.71) * mm});
            skLineSegment(sketch, "E51.3.6.2", {"start": v(13.67, 65.71) * mm, "end": v(13.67, 59.38) * mm});
            skLineSegment(sketch, "E51.3.6.3", {"start": v(13.67, 59.38) * mm, "end": v(0, 59.38) * mm});
            skLineSegment(sketch, "E51.3.7.0", {"start": v(0, 53.05) * mm, "end": v(13.67, 53.05) * mm});
            skLineSegment(sketch, "E51.3.7.1", {"start": v(0, 46.72) * mm, "end": v(0, 53.05) * mm});
            skLineSegment(sketch, "E51.3.7.2", {"start": v(13.67, 53.05) * mm, "end": v(13.67, 46.72) * mm});
            skLineSegment(sketch, "E51.3.7.3", {"start": v(13.67, 46.72) * mm, "end": v(0, 46.72) * mm});
            skLineSegment(sketch, "E51.4.0.0", {"start": v(27.33, 141.7) * mm, "end": v(41, 141.7) * mm});
            skLineSegment(sketch, "E51.4.0.1", {"start": v(27.33, 135.36) * mm, "end": v(27.33, 141.7) * mm});
            skLineSegment(sketch, "E51.4.0.2", {"start": v(41, 141.7) * mm, "end": v(41, 135.36) * mm});
            skLineSegment(sketch, "E51.4.0.3", {"start": v(41, 135.36) * mm, "end": v(27.33, 135.36) * mm});
            skLineSegment(sketch, "E51.4.1.0", {"start": v(27.33, 129.03) * mm, "end": v(41, 129.03) * mm});
            skLineSegment(sketch, "E51.4.1.1", {"start": v(27.33, 122.7) * mm, "end": v(27.33, 129.03) * mm});
            skLineSegment(sketch, "E51.4.1.2", {"start": v(41, 129.03) * mm, "end": v(41, 122.7) * mm});
            skLineSegment(sketch, "E51.4.1.3", {"start": v(41, 122.7) * mm, "end": v(27.33, 122.7) * mm});
            skLineSegment(sketch, "E51.4.2.0", {"start": v(27.33, 116.37) * mm, "end": v(41, 116.37) * mm});
            skLineSegment(sketch, "E51.4.2.1", {"start": v(27.33, 110.03) * mm, "end": v(27.33, 116.37) * mm});
            skLineSegment(sketch, "E51.4.2.2", {"start": v(41, 116.37) * mm, "end": v(41, 110.03) * mm});
            skLineSegment(sketch, "E51.4.2.3", {"start": v(41, 110.03) * mm, "end": v(27.33, 110.03) * mm});
            skLineSegment(sketch, "E51.4.3.0", {"start": v(27.33, 103.7) * mm, "end": v(41, 103.7) * mm});
            skLineSegment(sketch, "E51.4.3.1", {"start": v(27.33, 97.37) * mm, "end": v(27.33, 103.7) * mm});
            skLineSegment(sketch, "E51.4.3.2", {"start": v(41, 103.7) * mm, "end": v(41, 97.37) * mm});
            skLineSegment(sketch, "E51.4.3.3", {"start": v(41, 97.37) * mm, "end": v(27.33, 97.37) * mm});
            skLineSegment(sketch, "E51.4.4.0", {"start": v(27.33, 91.04) * mm, "end": v(41, 91.04) * mm});
            skLineSegment(sketch, "E51.4.4.1", {"start": v(27.33, 84.7) * mm, "end": v(27.33, 91.04) * mm});
            skLineSegment(sketch, "E51.4.4.2", {"start": v(41, 91.04) * mm, "end": v(41, 84.7) * mm});
            skLineSegment(sketch, "E51.4.4.3", {"start": v(41, 84.7) * mm, "end": v(27.33, 84.7) * mm});
            skLineSegment(sketch, "E51.4.5.0", {"start": v(27.33, 78.38) * mm, "end": v(41, 78.38) * mm});
            skLineSegment(sketch, "E51.4.5.1", {"start": v(27.33, 72.04) * mm, "end": v(27.33, 78.38) * mm});
            skLineSegment(sketch, "E51.4.5.2", {"start": v(41, 78.38) * mm, "end": v(41, 72.04) * mm});
            skLineSegment(sketch, "E51.4.5.3", {"start": v(41, 72.04) * mm, "end": v(27.33, 72.04) * mm});
            skLineSegment(sketch, "E51.4.6.0", {"start": v(27.33, 65.71) * mm, "end": v(41, 65.71) * mm});
            skLineSegment(sketch, "E51.4.6.1", {"start": v(27.33, 59.38) * mm, "end": v(27.33, 65.71) * mm});
            skLineSegment(sketch, "E51.4.6.2", {"start": v(41, 65.71) * mm, "end": v(41, 59.38) * mm});
            skLineSegment(sketch, "E51.4.6.3", {"start": v(41, 59.38) * mm, "end": v(27.33, 59.38) * mm});
            skLineSegment(sketch, "E51.4.7.0", {"start": v(27.33, 53.05) * mm, "end": v(41, 53.05) * mm});
            skLineSegment(sketch, "E51.4.7.1", {"start": v(27.33, 46.72) * mm, "end": v(27.33, 53.05) * mm});
            skLineSegment(sketch, "E51.4.7.2", {"start": v(41, 53.05) * mm, "end": v(41, 46.72) * mm});
            skLineSegment(sketch, "E51.4.7.3", {"start": v(41, 46.72) * mm, "end": v(27.33, 46.72) * mm});
            skLineSegment(sketch, "E51.5.0.0", {"start": v(54.67, 141.7) * mm, "end": v(68.33, 141.7) * mm});
            skLineSegment(sketch, "E51.5.0.1", {"start": v(54.67, 135.36) * mm, "end": v(54.67, 141.7) * mm});
            skLineSegment(sketch, "E51.5.0.2", {"start": v(68.33, 141.7) * mm, "end": v(68.33, 135.36) * mm});
            skLineSegment(sketch, "E51.5.0.3", {"start": v(68.33, 135.36) * mm, "end": v(54.67, 135.36) * mm});
            skLineSegment(sketch, "E51.5.1.0", {"start": v(54.67, 129.03) * mm, "end": v(68.33, 129.03) * mm});
            skLineSegment(sketch, "E51.5.1.1", {"start": v(54.67, 122.7) * mm, "end": v(54.67, 129.03) * mm});
            skLineSegment(sketch, "E51.5.1.2", {"start": v(68.33, 129.03) * mm, "end": v(68.33, 122.7) * mm});
            skLineSegment(sketch, "E51.5.1.3", {"start": v(68.33, 122.7) * mm, "end": v(54.67, 122.7) * mm});
            skLineSegment(sketch, "E51.5.2.0", {"start": v(54.67, 116.37) * mm, "end": v(68.33, 116.37) * mm});
            skLineSegment(sketch, "E51.5.2.1", {"start": v(54.67, 110.03) * mm, "end": v(54.67, 116.37) * mm});
            skLineSegment(sketch, "E51.5.2.2", {"start": v(68.33, 116.37) * mm, "end": v(68.33, 110.03) * mm});
            skLineSegment(sketch, "E51.5.2.3", {"start": v(68.33, 110.03) * mm, "end": v(54.67, 110.03) * mm});
            skLineSegment(sketch, "E51.5.3.0", {"start": v(54.67, 103.7) * mm, "end": v(68.33, 103.7) * mm});
            skLineSegment(sketch, "E51.5.3.1", {"start": v(54.67, 97.37) * mm, "end": v(54.67, 103.7) * mm});
            skLineSegment(sketch, "E51.5.3.2", {"start": v(68.33, 103.7) * mm, "end": v(68.33, 97.37) * mm});
            skLineSegment(sketch, "E51.5.3.3", {"start": v(68.33, 97.37) * mm, "end": v(54.67, 97.37) * mm});
            skLineSegment(sketch, "E51.5.4.0", {"start": v(54.67, 91.04) * mm, "end": v(68.33, 91.04) * mm});
            skLineSegment(sketch, "E51.5.4.1", {"start": v(54.67, 84.7) * mm, "end": v(54.67, 91.04) * mm});
            skLineSegment(sketch, "E51.5.4.2", {"start": v(68.33, 91.04) * mm, "end": v(68.33, 84.7) * mm});
            skLineSegment(sketch, "E51.5.4.3", {"start": v(68.33, 84.7) * mm, "end": v(54.67, 84.7) * mm});
            skLineSegment(sketch, "E51.5.5.0", {"start": v(54.67, 78.38) * mm, "end": v(68.33, 78.38) * mm});
            skLineSegment(sketch, "E51.5.5.1", {"start": v(54.67, 72.04) * mm, "end": v(54.67, 78.38) * mm});
            skLineSegment(sketch, "E51.5.5.2", {"start": v(68.33, 78.38) * mm, "end": v(68.33, 72.04) * mm});
            skLineSegment(sketch, "E51.5.5.3", {"start": v(68.33, 72.04) * mm, "end": v(54.67, 72.04) * mm});
            skLineSegment(sketch, "E51.5.6.0", {"start": v(54.67, 65.71) * mm, "end": v(68.33, 65.71) * mm});
            skLineSegment(sketch, "E51.5.6.1", {"start": v(54.67, 59.38) * mm, "end": v(54.67, 65.71) * mm});
            skLineSegment(sketch, "E51.5.6.2", {"start": v(68.33, 65.71) * mm, "end": v(68.33, 59.38) * mm});
            skLineSegment(sketch, "E51.5.6.3", {"start": v(68.33, 59.38) * mm, "end": v(54.67, 59.38) * mm});
            skLineSegment(sketch, "E51.5.7.0", {"start": v(54.67, 53.05) * mm, "end": v(68.33, 53.05) * mm});
            skLineSegment(sketch, "E51.5.7.1", {"start": v(54.67, 46.72) * mm, "end": v(54.67, 53.05) * mm});
            skLineSegment(sketch, "E51.5.7.2", {"start": v(68.33, 53.05) * mm, "end": v(68.33, 46.72) * mm});
            skLineSegment(sketch, "E51.5.7.3", {"start": v(68.33, 46.72) * mm, "end": v(54.67, 46.72) * mm});
            skLineSegment(sketch, "E51.direction1", {"start": v(-82, 141.7) * mm, "end": v(-54.67, 141.7) * mm, "construction": true});
            skLineSegment(sketch, "E51.direction2", {"start": v(-82, 141.7) * mm, "end": v(-82, 129.03) * mm, "construction": true});
            skLineSegment(sketch, "E52.bottom", {"start": v(-68.33, 135.36) * mm, "end": v(-54.67, 135.36) * mm});
            skLineSegment(sketch, "E52.top", {"start": v(-68.33, 129.03) * mm, "end": v(-54.67, 129.03) * mm});
            skLineSegment(sketch, "E52.left", {"start": v(-68.33, 135.36) * mm, "end": v(-68.33, 129.03) * mm});
            skLineSegment(sketch, "E52.right", {"start": v(-54.67, 135.36) * mm, "end": v(-54.67, 129.03) * mm});
            skLineSegment(sketch, "E53.0.1.0", {"start": v(-68.33, 122.7) * mm, "end": v(-68.33, 116.37) * mm});
            skLineSegment(sketch, "E53.0.1.1", {"start": v(-68.33, 122.7) * mm, "end": v(-54.67, 122.7) * mm});
            skLineSegment(sketch, "E53.0.1.2", {"start": v(-68.33, 116.37) * mm, "end": v(-54.67, 116.37) * mm});
            skLineSegment(sketch, "E53.0.1.3", {"start": v(-54.67, 122.7) * mm, "end": v(-54.67, 116.37) * mm});
            skLineSegment(sketch, "E53.0.2.0", {"start": v(-68.33, 110.03) * mm, "end": v(-68.33, 103.7) * mm});
            skLineSegment(sketch, "E53.0.2.1", {"start": v(-68.33, 110.03) * mm, "end": v(-54.67, 110.03) * mm});
            skLineSegment(sketch, "E53.0.2.2", {"start": v(-68.33, 103.7) * mm, "end": v(-54.67, 103.7) * mm});
            skLineSegment(sketch, "E53.0.2.3", {"start": v(-54.67, 110.03) * mm, "end": v(-54.67, 103.7) * mm});
            skLineSegment(sketch, "E53.0.3.0", {"start": v(-68.33, 97.37) * mm, "end": v(-68.33, 91.04) * mm});
            skLineSegment(sketch, "E53.0.3.1", {"start": v(-68.33, 97.37) * mm, "end": v(-54.67, 97.37) * mm});
            skLineSegment(sketch, "E53.0.3.2", {"start": v(-68.33, 91.04) * mm, "end": v(-54.67, 91.04) * mm});
            skLineSegment(sketch, "E53.0.3.3", {"start": v(-54.67, 97.37) * mm, "end": v(-54.67, 91.04) * mm});
            skLineSegment(sketch, "E53.0.4.0", {"start": v(-68.33, 84.7) * mm, "end": v(-68.33, 78.38) * mm});
            skLineSegment(sketch, "E53.0.4.1", {"start": v(-68.33, 84.7) * mm, "end": v(-54.67, 84.7) * mm});
            skLineSegment(sketch, "E53.0.4.2", {"start": v(-68.33, 78.38) * mm, "end": v(-54.67, 78.38) * mm});
            skLineSegment(sketch, "E53.0.4.3", {"start": v(-54.67, 84.7) * mm, "end": v(-54.67, 78.38) * mm});
            skLineSegment(sketch, "E53.0.5.0", {"start": v(-68.33, 72.04) * mm, "end": v(-68.33, 65.71) * mm});
            skLineSegment(sketch, "E53.0.5.1", {"start": v(-68.33, 72.04) * mm, "end": v(-54.67, 72.04) * mm});
            skLineSegment(sketch, "E53.0.5.2", {"start": v(-68.33, 65.71) * mm, "end": v(-54.67, 65.71) * mm});
            skLineSegment(sketch, "E53.0.5.3", {"start": v(-54.67, 72.04) * mm, "end": v(-54.67, 65.71) * mm});
            skLineSegment(sketch, "E53.0.6.0", {"start": v(-68.33, 59.38) * mm, "end": v(-68.33, 53.05) * mm});
            skLineSegment(sketch, "E53.0.6.1", {"start": v(-68.33, 59.38) * mm, "end": v(-54.67, 59.38) * mm});
            skLineSegment(sketch, "E53.0.6.2", {"start": v(-68.33, 53.05) * mm, "end": v(-54.67, 53.05) * mm});
            skLineSegment(sketch, "E53.0.6.3", {"start": v(-54.67, 59.38) * mm, "end": v(-54.67, 53.05) * mm});
            skLineSegment(sketch, "E53.1.0.0", {"start": v(-41, 135.36) * mm, "end": v(-41, 129.03) * mm});
            skLineSegment(sketch, "E53.1.0.1", {"start": v(-41, 135.36) * mm, "end": v(-27.33, 135.36) * mm});
            skLineSegment(sketch, "E53.1.0.2", {"start": v(-41, 129.03) * mm, "end": v(-27.33, 129.03) * mm});
            skLineSegment(sketch, "E53.1.0.3", {"start": v(-27.33, 135.36) * mm, "end": v(-27.33, 129.03) * mm});
            skLineSegment(sketch, "E53.1.1.0", {"start": v(-41, 122.7) * mm, "end": v(-41, 116.37) * mm});
            skLineSegment(sketch, "E53.1.1.1", {"start": v(-41, 122.7) * mm, "end": v(-27.33, 122.7) * mm});
            skLineSegment(sketch, "E53.1.1.2", {"start": v(-41, 116.37) * mm, "end": v(-27.33, 116.37) * mm});
            skLineSegment(sketch, "E53.1.1.3", {"start": v(-27.33, 122.7) * mm, "end": v(-27.33, 116.37) * mm});
            skLineSegment(sketch, "E53.1.2.0", {"start": v(-41, 110.03) * mm, "end": v(-41, 103.7) * mm});
            skLineSegment(sketch, "E53.1.2.1", {"start": v(-41, 110.03) * mm, "end": v(-27.33, 110.03) * mm});
            skLineSegment(sketch, "E53.1.2.2", {"start": v(-41, 103.7) * mm, "end": v(-27.33, 103.7) * mm});
            skLineSegment(sketch, "E53.1.2.3", {"start": v(-27.33, 110.03) * mm, "end": v(-27.33, 103.7) * mm});
            skLineSegment(sketch, "E53.1.3.0", {"start": v(-41, 97.37) * mm, "end": v(-41, 91.04) * mm});
            skLineSegment(sketch, "E53.1.3.1", {"start": v(-41, 97.37) * mm, "end": v(-27.33, 97.37) * mm});
            skLineSegment(sketch, "E53.1.3.2", {"start": v(-41, 91.04) * mm, "end": v(-27.33, 91.04) * mm});
            skLineSegment(sketch, "E53.1.3.3", {"start": v(-27.33, 97.37) * mm, "end": v(-27.33, 91.04) * mm});
            skLineSegment(sketch, "E53.1.4.0", {"start": v(-41, 84.7) * mm, "end": v(-41, 78.38) * mm});
            skLineSegment(sketch, "E53.1.4.1", {"start": v(-41, 84.7) * mm, "end": v(-27.33, 84.7) * mm});
            skLineSegment(sketch, "E53.1.4.2", {"start": v(-41, 78.38) * mm, "end": v(-27.33, 78.38) * mm});
            skLineSegment(sketch, "E53.1.4.3", {"start": v(-27.33, 84.7) * mm, "end": v(-27.33, 78.38) * mm});
            skLineSegment(sketch, "E53.1.5.0", {"start": v(-41, 72.04) * mm, "end": v(-41, 65.71) * mm});
            skLineSegment(sketch, "E53.1.5.1", {"start": v(-41, 72.04) * mm, "end": v(-27.33, 72.04) * mm});
            skLineSegment(sketch, "E53.1.5.2", {"start": v(-41, 65.71) * mm, "end": v(-27.33, 65.71) * mm});
            skLineSegment(sketch, "E53.1.5.3", {"start": v(-27.33, 72.04) * mm, "end": v(-27.33, 65.71) * mm});
            skLineSegment(sketch, "E53.1.6.0", {"start": v(-41, 59.38) * mm, "end": v(-41, 53.05) * mm});
            skLineSegment(sketch, "E53.1.6.1", {"start": v(-41, 59.38) * mm, "end": v(-27.33, 59.38) * mm});
            skLineSegment(sketch, "E53.1.6.2", {"start": v(-41, 53.05) * mm, "end": v(-27.33, 53.05) * mm});
            skLineSegment(sketch, "E53.1.6.3", {"start": v(-27.33, 59.38) * mm, "end": v(-27.33, 53.05) * mm});
            skLineSegment(sketch, "E53.2.0.0", {"start": v(-13.67, 135.36) * mm, "end": v(-13.67, 129.03) * mm});
            skLineSegment(sketch, "E53.2.0.1", {"start": v(-13.67, 135.36) * mm, "end": v(0, 135.36) * mm});
            skLineSegment(sketch, "E53.2.0.2", {"start": v(-13.67, 129.03) * mm, "end": v(0, 129.03) * mm});
            skLineSegment(sketch, "E53.2.0.3", {"start": v(0, 135.36) * mm, "end": v(0, 129.03) * mm});
            skLineSegment(sketch, "E53.2.1.0", {"start": v(-13.67, 122.7) * mm, "end": v(-13.67, 116.37) * mm});
            skLineSegment(sketch, "E53.2.1.1", {"start": v(-13.67, 122.7) * mm, "end": v(0, 122.7) * mm});
            skLineSegment(sketch, "E53.2.1.2", {"start": v(-13.67, 116.37) * mm, "end": v(0, 116.37) * mm});
            skLineSegment(sketch, "E53.2.1.3", {"start": v(0, 122.7) * mm, "end": v(0, 116.37) * mm});
            skLineSegment(sketch, "E53.2.2.0", {"start": v(-13.67, 110.03) * mm, "end": v(-13.67, 103.7) * mm});
            skLineSegment(sketch, "E53.2.2.1", {"start": v(-13.67, 110.03) * mm, "end": v(0, 110.03) * mm});
            skLineSegment(sketch, "E53.2.2.2", {"start": v(-13.67, 103.7) * mm, "end": v(0, 103.7) * mm});
            skLineSegment(sketch, "E53.2.2.3", {"start": v(0, 110.03) * mm, "end": v(0, 103.7) * mm});
            skLineSegment(sketch, "E53.2.3.0", {"start": v(-13.67, 97.37) * mm, "end": v(-13.67, 91.04) * mm});
            skLineSegment(sketch, "E53.2.3.1", {"start": v(-13.67, 97.37) * mm, "end": v(0, 97.37) * mm});
            skLineSegment(sketch, "E53.2.3.2", {"start": v(-13.67, 91.04) * mm, "end": v(0, 91.04) * mm});
            skLineSegment(sketch, "E53.2.3.3", {"start": v(0, 97.37) * mm, "end": v(0, 91.04) * mm});
            skLineSegment(sketch, "E53.2.4.0", {"start": v(-13.67, 84.7) * mm, "end": v(-13.67, 78.38) * mm});
            skLineSegment(sketch, "E53.2.4.1", {"start": v(-13.67, 84.7) * mm, "end": v(0, 84.7) * mm});
            skLineSegment(sketch, "E53.2.4.2", {"start": v(-13.67, 78.38) * mm, "end": v(0, 78.38) * mm});
            skLineSegment(sketch, "E53.2.4.3", {"start": v(0, 84.7) * mm, "end": v(0, 78.38) * mm});
            skLineSegment(sketch, "E53.2.5.0", {"start": v(-13.67, 72.04) * mm, "end": v(-13.67, 65.71) * mm});
            skLineSegment(sketch, "E53.2.5.1", {"start": v(-13.67, 72.04) * mm, "end": v(0, 72.04) * mm});
            skLineSegment(sketch, "E53.2.5.2", {"start": v(-13.67, 65.71) * mm, "end": v(0, 65.71) * mm});
            skLineSegment(sketch, "E53.2.5.3", {"start": v(0, 72.04) * mm, "end": v(0, 65.71) * mm});
            skLineSegment(sketch, "E53.2.6.0", {"start": v(-13.67, 59.38) * mm, "end": v(-13.67, 53.05) * mm});
            skLineSegment(sketch, "E53.2.6.1", {"start": v(-13.67, 59.38) * mm, "end": v(0, 59.38) * mm});
            skLineSegment(sketch, "E53.2.6.2", {"start": v(-13.67, 53.05) * mm, "end": v(0, 53.05) * mm});
            skLineSegment(sketch, "E53.2.6.3", {"start": v(0, 59.38) * mm, "end": v(0, 53.05) * mm});
            skLineSegment(sketch, "E53.3.0.0", {"start": v(13.67, 135.36) * mm, "end": v(13.67, 129.03) * mm});
            skLineSegment(sketch, "E53.3.0.1", {"start": v(13.67, 135.36) * mm, "end": v(27.33, 135.36) * mm});
            skLineSegment(sketch, "E53.3.0.2", {"start": v(13.67, 129.03) * mm, "end": v(27.33, 129.03) * mm});
            skLineSegment(sketch, "E53.3.0.3", {"start": v(27.33, 135.36) * mm, "end": v(27.33, 129.03) * mm});
            skLineSegment(sketch, "E53.3.1.0", {"start": v(13.67, 122.7) * mm, "end": v(13.67, 116.37) * mm});
            skLineSegment(sketch, "E53.3.1.1", {"start": v(13.67, 122.7) * mm, "end": v(27.33, 122.7) * mm});
            skLineSegment(sketch, "E53.3.1.2", {"start": v(13.67, 116.37) * mm, "end": v(27.33, 116.37) * mm});
            skLineSegment(sketch, "E53.3.1.3", {"start": v(27.33, 122.7) * mm, "end": v(27.33, 116.37) * mm});
            skLineSegment(sketch, "E53.3.2.0", {"start": v(13.67, 110.03) * mm, "end": v(13.67, 103.7) * mm});
            skLineSegment(sketch, "E53.3.2.1", {"start": v(13.67, 110.03) * mm, "end": v(27.33, 110.03) * mm});
            skLineSegment(sketch, "E53.3.2.2", {"start": v(13.67, 103.7) * mm, "end": v(27.33, 103.7) * mm});
            skLineSegment(sketch, "E53.3.2.3", {"start": v(27.33, 110.03) * mm, "end": v(27.33, 103.7) * mm});
            skLineSegment(sketch, "E53.3.3.0", {"start": v(13.67, 97.37) * mm, "end": v(13.67, 91.04) * mm});
            skLineSegment(sketch, "E53.3.3.1", {"start": v(13.67, 97.37) * mm, "end": v(27.33, 97.37) * mm});
            skLineSegment(sketch, "E53.3.3.2", {"start": v(13.67, 91.04) * mm, "end": v(27.33, 91.04) * mm});
            skLineSegment(sketch, "E53.3.3.3", {"start": v(27.33, 97.37) * mm, "end": v(27.33, 91.04) * mm});
            skLineSegment(sketch, "E53.3.4.0", {"start": v(13.67, 84.7) * mm, "end": v(13.67, 78.38) * mm});
            skLineSegment(sketch, "E53.3.4.1", {"start": v(13.67, 84.7) * mm, "end": v(27.33, 84.7) * mm});
            skLineSegment(sketch, "E53.3.4.2", {"start": v(13.67, 78.38) * mm, "end": v(27.33, 78.38) * mm});
            skLineSegment(sketch, "E53.3.4.3", {"start": v(27.33, 84.7) * mm, "end": v(27.33, 78.38) * mm});
            skLineSegment(sketch, "E53.3.5.0", {"start": v(13.67, 72.04) * mm, "end": v(13.67, 65.71) * mm});
            skLineSegment(sketch, "E53.3.5.1", {"start": v(13.67, 72.04) * mm, "end": v(27.33, 72.04) * mm});
            skLineSegment(sketch, "E53.3.5.2", {"start": v(13.67, 65.71) * mm, "end": v(27.33, 65.71) * mm});
            skLineSegment(sketch, "E53.3.5.3", {"start": v(27.33, 72.04) * mm, "end": v(27.33, 65.71) * mm});
            skLineSegment(sketch, "E53.3.6.0", {"start": v(13.67, 59.38) * mm, "end": v(13.67, 53.05) * mm});
            skLineSegment(sketch, "E53.3.6.1", {"start": v(13.67, 59.38) * mm, "end": v(27.33, 59.38) * mm});
            skLineSegment(sketch, "E53.3.6.2", {"start": v(13.67, 53.05) * mm, "end": v(27.33, 53.05) * mm});
            skLineSegment(sketch, "E53.3.6.3", {"start": v(27.33, 59.38) * mm, "end": v(27.33, 53.05) * mm});
            skLineSegment(sketch, "E53.4.0.0", {"start": v(41, 135.36) * mm, "end": v(41, 129.03) * mm});
            skLineSegment(sketch, "E53.4.0.1", {"start": v(41, 135.36) * mm, "end": v(54.67, 135.36) * mm});
            skLineSegment(sketch, "E53.4.0.2", {"start": v(41, 129.03) * mm, "end": v(54.67, 129.03) * mm});
            skLineSegment(sketch, "E53.4.0.3", {"start": v(54.67, 135.36) * mm, "end": v(54.67, 129.03) * mm});
            skLineSegment(sketch, "E53.4.1.0", {"start": v(41, 122.7) * mm, "end": v(41, 116.37) * mm});
            skLineSegment(sketch, "E53.4.1.1", {"start": v(41, 122.7) * mm, "end": v(54.67, 122.7) * mm});
            skLineSegment(sketch, "E53.4.1.2", {"start": v(41, 116.37) * mm, "end": v(54.67, 116.37) * mm});
            skLineSegment(sketch, "E53.4.1.3", {"start": v(54.67, 122.7) * mm, "end": v(54.67, 116.37) * mm});
            skLineSegment(sketch, "E53.4.2.0", {"start": v(41, 110.03) * mm, "end": v(41, 103.7) * mm});
            skLineSegment(sketch, "E53.4.2.1", {"start": v(41, 110.03) * mm, "end": v(54.67, 110.03) * mm});
            skLineSegment(sketch, "E53.4.2.2", {"start": v(41, 103.7) * mm, "end": v(54.67, 103.7) * mm});
            skLineSegment(sketch, "E53.4.2.3", {"start": v(54.67, 110.03) * mm, "end": v(54.67, 103.7) * mm});
            skLineSegment(sketch, "E53.4.3.0", {"start": v(41, 97.37) * mm, "end": v(41, 91.04) * mm});
            skLineSegment(sketch, "E53.4.3.1", {"start": v(41, 97.37) * mm, "end": v(54.67, 97.37) * mm});
            skLineSegment(sketch, "E53.4.3.2", {"start": v(41, 91.04) * mm, "end": v(54.67, 91.04) * mm});
            skLineSegment(sketch, "E53.4.3.3", {"start": v(54.67, 97.37) * mm, "end": v(54.67, 91.04) * mm});
            skLineSegment(sketch, "E53.4.4.0", {"start": v(41, 84.7) * mm, "end": v(41, 78.38) * mm});
            skLineSegment(sketch, "E53.4.4.1", {"start": v(41, 84.7) * mm, "end": v(54.67, 84.7) * mm});
            skLineSegment(sketch, "E53.4.4.2", {"start": v(41, 78.38) * mm, "end": v(54.67, 78.38) * mm});
            skLineSegment(sketch, "E53.4.4.3", {"start": v(54.67, 84.7) * mm, "end": v(54.67, 78.38) * mm});
            skLineSegment(sketch, "E53.4.5.0", {"start": v(41, 72.04) * mm, "end": v(41, 65.71) * mm});
            skLineSegment(sketch, "E53.4.5.1", {"start": v(41, 72.04) * mm, "end": v(54.67, 72.04) * mm});
            skLineSegment(sketch, "E53.4.5.2", {"start": v(41, 65.71) * mm, "end": v(54.67, 65.71) * mm});
            skLineSegment(sketch, "E53.4.5.3", {"start": v(54.67, 72.04) * mm, "end": v(54.67, 65.71) * mm});
            skLineSegment(sketch, "E53.4.6.0", {"start": v(41, 59.38) * mm, "end": v(41, 53.05) * mm});
            skLineSegment(sketch, "E53.4.6.1", {"start": v(41, 59.38) * mm, "end": v(54.67, 59.38) * mm});
            skLineSegment(sketch, "E53.4.6.2", {"start": v(41, 53.05) * mm, "end": v(54.67, 53.05) * mm});
            skLineSegment(sketch, "E53.4.6.3", {"start": v(54.67, 59.38) * mm, "end": v(54.67, 53.05) * mm});
            skLineSegment(sketch, "E53.5.0.0", {"start": v(68.33, 135.36) * mm, "end": v(68.33, 129.03) * mm});
            skLineSegment(sketch, "E53.5.0.1", {"start": v(68.33, 135.36) * mm, "end": v(82, 135.36) * mm});
            skLineSegment(sketch, "E53.5.0.2", {"start": v(68.33, 129.03) * mm, "end": v(82, 129.03) * mm});
            skLineSegment(sketch, "E53.5.0.3", {"start": v(82, 135.36) * mm, "end": v(82, 129.03) * mm});
            skLineSegment(sketch, "E53.5.1.0", {"start": v(68.33, 122.7) * mm, "end": v(68.33, 116.37) * mm});
            skLineSegment(sketch, "E53.5.1.1", {"start": v(68.33, 122.7) * mm, "end": v(82, 122.7) * mm});
            skLineSegment(sketch, "E53.5.1.2", {"start": v(68.33, 116.37) * mm, "end": v(82, 116.37) * mm});
            skLineSegment(sketch, "E53.5.1.3", {"start": v(82, 122.7) * mm, "end": v(82, 116.37) * mm});
            skLineSegment(sketch, "E53.5.2.0", {"start": v(68.33, 110.03) * mm, "end": v(68.33, 103.7) * mm});
            skLineSegment(sketch, "E53.5.2.1", {"start": v(68.33, 110.03) * mm, "end": v(82, 110.03) * mm});
            skLineSegment(sketch, "E53.5.2.2", {"start": v(68.33, 103.7) * mm, "end": v(82, 103.7) * mm});
            skLineSegment(sketch, "E53.5.2.3", {"start": v(82, 110.03) * mm, "end": v(82, 103.7) * mm});
            skLineSegment(sketch, "E53.5.3.0", {"start": v(68.33, 97.37) * mm, "end": v(68.33, 91.04) * mm});
            skLineSegment(sketch, "E53.5.3.1", {"start": v(68.33, 97.37) * mm, "end": v(82, 97.37) * mm});
            skLineSegment(sketch, "E53.5.3.2", {"start": v(68.33, 91.04) * mm, "end": v(82, 91.04) * mm});
            skLineSegment(sketch, "E53.5.3.3", {"start": v(82, 97.37) * mm, "end": v(82, 91.04) * mm});
            skLineSegment(sketch, "E53.5.4.0", {"start": v(68.33, 84.7) * mm, "end": v(68.33, 78.38) * mm});
            skLineSegment(sketch, "E53.5.4.1", {"start": v(68.33, 84.7) * mm, "end": v(82, 84.7) * mm});
            skLineSegment(sketch, "E53.5.4.2", {"start": v(68.33, 78.38) * mm, "end": v(82, 78.38) * mm});
            skLineSegment(sketch, "E53.5.4.3", {"start": v(82, 84.7) * mm, "end": v(82, 78.38) * mm});
            skLineSegment(sketch, "E53.5.5.0", {"start": v(68.33, 72.04) * mm, "end": v(68.33, 65.71) * mm});
            skLineSegment(sketch, "E53.5.5.1", {"start": v(68.33, 72.04) * mm, "end": v(82, 72.04) * mm});
            skLineSegment(sketch, "E53.5.5.2", {"start": v(68.33, 65.71) * mm, "end": v(82, 65.71) * mm});
            skLineSegment(sketch, "E53.5.5.3", {"start": v(82, 72.04) * mm, "end": v(82, 65.71) * mm});
            skLineSegment(sketch, "E53.5.6.0", {"start": v(68.33, 59.38) * mm, "end": v(68.33, 53.05) * mm});
            skLineSegment(sketch, "E53.5.6.1", {"start": v(68.33, 59.38) * mm, "end": v(82, 59.38) * mm});
            skLineSegment(sketch, "E53.5.6.2", {"start": v(68.33, 53.05) * mm, "end": v(82, 53.05) * mm});
            skLineSegment(sketch, "E53.5.6.3", {"start": v(82, 59.38) * mm, "end": v(82, 53.05) * mm});
            skLineSegment(sketch, "E53.direction1", {"start": v(-68.33, 129.03) * mm, "end": v(-41, 129.03) * mm, "construction": true});
            skLineSegment(sketch, "E53.direction2", {"start": v(-68.33, 129.03) * mm, "end": v(-68.33, 116.37) * mm, "construction": true});
            skSolve(sketch);
        }
        {
            var Q0;
            {var subQ3=sQuery(id+"F16.wireOp",EDGE,"E53.0.3.1");Q0=makeQuery(id+"F16.imprint","IMPRINT",FACE,{"disambiguationData":[TD([[makeQuery(id+"F16.imprint","IMPRINT",EDGE,{"derivedFrom":subQ3}),-1.0]])]});}
            var Q1;
            {var subQ0=sQuery(id+"F16.wireOp",EDGE,"E53.0.4.1");Q1=makeQuery(id+"F16.imprint","IMPRINT",FACE,{"disambiguationData":[TD([[makeQuery(id+"F16.imprint","IMPRINT",EDGE,{"derivedFrom":subQ0}),-1.0]])]});}
            var Q2;
            {var subQ3=sQuery(id+"F16.wireOp",EDGE,"E53.0.5.1");Q2=makeQuery(id+"F16.imprint","IMPRINT",FACE,{"disambiguationData":[TD([[makeQuery(id+"F16.imprint","IMPRINT",EDGE,{"derivedFrom":subQ3}),-1.0]])]});}
            var Q3;
            {var subQ1=sQuery(id+"F16.wireOp",EDGE,"E53.0.6.1");Q3=makeQuery(id+"F16.imprint","IMPRINT",FACE,{"disambiguationData":[TD([[makeQuery(id+"F16.imprint","IMPRINT",EDGE,{"derivedFrom":subQ1}),-1.0]])]});}
            var Q4;
            Q4=makeQuery(id+"F16.imprint","IMPRINT",FACE,{"disambiguationData":[TD([[makeQuery(id+"F16.imprint","IMPRINT",EDGE,{"derivedFrom":sQuery(id+"F16.wireOp",EDGE,"E53.1.0.0")}),1.0]])]});
            var Q5;
            {var subQ1=sQuery(id+"F16.wireOp",EDGE,"E53.1.1.1");Q5=makeQuery(id+"F16.imprint","IMPRINT",FACE,{"disambiguationData":[TD([[makeQuery(id+"F16.imprint","IMPRINT",EDGE,{"derivedFrom":subQ1}),-1.0]])]});}
            var Q6;
            {var subQ3=sQuery(id+"F16.wireOp",EDGE,"E53.1.2.1");Q6=makeQuery(id+"F16.imprint","IMPRINT",FACE,{"disambiguationData":[TD([[makeQuery(id+"F16.imprint","IMPRINT",EDGE,{"derivedFrom":subQ3}),-1.0]])]});}
            var Q7;
            {var subQ0=sQuery(id+"F16.wireOp",EDGE,"E53.1.3.1");Q7=makeQuery(id+"F16.imprint","IMPRINT",FACE,{"disambiguationData":[TD([[makeQuery(id+"F16.imprint","IMPRINT",EDGE,{"derivedFrom":subQ0}),-1.0]])]});}
            var Q8;
            {var subQ3=sQuery(id+"F16.wireOp",EDGE,"E53.1.4.1");Q8=makeQuery(id+"F16.imprint","IMPRINT",FACE,{"disambiguationData":[TD([[makeQuery(id+"F16.imprint","IMPRINT",EDGE,{"derivedFrom":subQ3}),-1.0]])]});}
            var Q9;
            {var subQ1=sQuery(id+"F16.wireOp",EDGE,"E53.1.5.1");Q9=makeQuery(id+"F16.imprint","IMPRINT",FACE,{"disambiguationData":[TD([[makeQuery(id+"F16.imprint","IMPRINT",EDGE,{"derivedFrom":subQ1}),-1.0]])]});}
            var Q10;
            {var subQ1=sQuery(id+"F16.wireOp",EDGE,"E53.1.6.1");Q10=makeQuery(id+"F16.imprint","IMPRINT",FACE,{"disambiguationData":[TD([[makeQuery(id+"F16.imprint","IMPRINT",EDGE,{"derivedFrom":subQ1}),-1.0]])]});}
            var Q11;
            Q11=makeQuery(id+"F16.imprint","IMPRINT",FACE,{"disambiguationData":[TD([[makeQuery(id+"F16.imprint","IMPRINT",EDGE,{"derivedFrom":sQuery(id+"F16.wireOp",EDGE,"E53.2.0.0")}),1.0]])]});
            var Q12;
            {var subQ3=sQuery(id+"F16.wireOp",EDGE,"E53.2.1.1");Q12=makeQuery(id+"F16.imprint","IMPRINT",FACE,{"disambiguationData":[TD([[makeQuery(id+"F16.imprint","IMPRINT",EDGE,{"derivedFrom":subQ3}),-1.0]])]});}
            var Q13;
            {var subQ0=sQuery(id+"F16.wireOp",EDGE,"E53.2.2.1");Q13=makeQuery(id+"F16.imprint","IMPRINT",FACE,{"disambiguationData":[TD([[makeQuery(id+"F16.imprint","IMPRINT",EDGE,{"derivedFrom":subQ0}),-1.0]])]});}
            var Q14;
            {var subQ1=sQuery(id+"F16.wireOp",EDGE,"E53.2.3.1");Q14=makeQuery(id+"F16.imprint","IMPRINT",FACE,{"disambiguationData":[TD([[makeQuery(id+"F16.imprint","IMPRINT",EDGE,{"derivedFrom":subQ1}),-1.0]])]});}
            var Q15;
            {var subQ1=sQuery(id+"F16.wireOp",EDGE,"E53.2.4.1");Q15=makeQuery(id+"F16.imprint","IMPRINT",FACE,{"disambiguationData":[TD([[makeQuery(id+"F16.imprint","IMPRINT",EDGE,{"derivedFrom":subQ1}),-1.0]])]});}
            var Q16;
            {var subQ3=sQuery(id+"F16.wireOp",EDGE,"E53.2.5.1");Q16=makeQuery(id+"F16.imprint","IMPRINT",FACE,{"disambiguationData":[TD([[makeQuery(id+"F16.imprint","IMPRINT",EDGE,{"derivedFrom":subQ3}),-1.0]])]});}
            var Q17;
            {var subQ3=sQuery(id+"F16.wireOp",EDGE,"E53.2.6.1");Q17=makeQuery(id+"F16.imprint","IMPRINT",FACE,{"disambiguationData":[TD([[makeQuery(id+"F16.imprint","IMPRINT",EDGE,{"derivedFrom":subQ3}),-1.0]])]});}
            var Q18;
            Q18=makeQuery(id+"F16.imprint","IMPRINT",FACE,{"disambiguationData":[TD([[makeQuery(id+"F16.imprint","IMPRINT",EDGE,{"derivedFrom":sQuery(id+"F16.wireOp",EDGE,"E53.3.0.0")}),1.0]])]});
            var Q19;
            {var subQ0=sQuery(id+"F16.wireOp",EDGE,"E53.3.1.1");Q19=makeQuery(id+"F16.imprint","IMPRINT",FACE,{"disambiguationData":[TD([[makeQuery(id+"F16.imprint","IMPRINT",EDGE,{"derivedFrom":subQ0}),-1.0]])]});}
            var Q20;
            {var subQ3=sQuery(id+"F16.wireOp",EDGE,"E53.3.2.1");Q20=makeQuery(id+"F16.imprint","IMPRINT",FACE,{"disambiguationData":[TD([[makeQuery(id+"F16.imprint","IMPRINT",EDGE,{"derivedFrom":subQ3}),-1.0]])]});}
            var Q21;
            {var subQ1=sQuery(id+"F16.wireOp",EDGE,"E53.3.3.1");Q21=makeQuery(id+"F16.imprint","IMPRINT",FACE,{"disambiguationData":[TD([[makeQuery(id+"F16.imprint","IMPRINT",EDGE,{"derivedFrom":subQ1}),-1.0]])]});}
            var Q22;
            {var subQ1=sQuery(id+"F16.wireOp",EDGE,"E53.3.4.1");Q22=makeQuery(id+"F16.imprint","IMPRINT",FACE,{"disambiguationData":[TD([[makeQuery(id+"F16.imprint","IMPRINT",EDGE,{"derivedFrom":subQ1}),-1.0]])]});}
            var Q23;
            {var subQ3=sQuery(id+"F16.wireOp",EDGE,"E53.3.5.1");Q23=makeQuery(id+"F16.imprint","IMPRINT",FACE,{"disambiguationData":[TD([[makeQuery(id+"F16.imprint","IMPRINT",EDGE,{"derivedFrom":subQ3}),-1.0]])]});}
            var Q24;
            {var subQ0=sQuery(id+"F16.wireOp",EDGE,"E53.3.6.1");Q24=makeQuery(id+"F16.imprint","IMPRINT",FACE,{"disambiguationData":[TD([[makeQuery(id+"F16.imprint","IMPRINT",EDGE,{"derivedFrom":subQ0}),-1.0]])]});}
            var Q25;
            Q25=makeQuery(id+"F16.imprint","IMPRINT",FACE,{"disambiguationData":[TD([[makeQuery(id+"F16.imprint","IMPRINT",EDGE,{"derivedFrom":sQuery(id+"F16.wireOp",EDGE,"E53.4.0.0")}),1.0]])]});
            var Q26;
            {var subQ1=sQuery(id+"F16.wireOp",EDGE,"E53.4.1.1");Q26=makeQuery(id+"F16.imprint","IMPRINT",FACE,{"disambiguationData":[TD([[makeQuery(id+"F16.imprint","IMPRINT",EDGE,{"derivedFrom":subQ1}),-1.0]])]});}
            var Q27;
            {var subQ1=sQuery(id+"F16.wireOp",EDGE,"E53.4.2.1");Q27=makeQuery(id+"F16.imprint","IMPRINT",FACE,{"disambiguationData":[TD([[makeQuery(id+"F16.imprint","IMPRINT",EDGE,{"derivedFrom":subQ1}),-1.0]])]});}
            var Q28;
            {var subQ0=sQuery(id+"F16.wireOp",EDGE,"E53.4.3.1");Q28=makeQuery(id+"F16.imprint","IMPRINT",FACE,{"disambiguationData":[TD([[makeQuery(id+"F16.imprint","IMPRINT",EDGE,{"derivedFrom":subQ0}),-1.0]])]});}
            var Q29;
            {var subQ3=sQuery(id+"F16.wireOp",EDGE,"E53.4.4.1");Q29=makeQuery(id+"F16.imprint","IMPRINT",FACE,{"disambiguationData":[TD([[makeQuery(id+"F16.imprint","IMPRINT",EDGE,{"derivedFrom":subQ3}),-1.0]])]});}
            var Q30;
            {var subQ0=sQuery(id+"F16.wireOp",EDGE,"E53.4.5.1");Q30=makeQuery(id+"F16.imprint","IMPRINT",FACE,{"disambiguationData":[TD([[makeQuery(id+"F16.imprint","IMPRINT",EDGE,{"derivedFrom":subQ0}),-1.0]])]});}
            var Q31;
            {var subQ1=sQuery(id+"F16.wireOp",EDGE,"E53.4.6.1");Q31=makeQuery(id+"F16.imprint","IMPRINT",FACE,{"disambiguationData":[TD([[makeQuery(id+"F16.imprint","IMPRINT",EDGE,{"derivedFrom":subQ1}),-1.0]])]});}
            var Q32;
            Q32=makeQuery(id+"F16.imprint","IMPRINT",FACE,{"disambiguationData":[TD([[makeQuery(id+"F16.imprint","IMPRINT",EDGE,{"derivedFrom":sQuery(id+"F16.wireOp",EDGE,"E52.bottom")}),-1.0]])]});
            var Q33;
            {var subQ3=sQuery(id+"F16.wireOp",EDGE,"E53.0.2.1");Q33=makeQuery(id+"F16.imprint","IMPRINT",FACE,{"disambiguationData":[TD([[makeQuery(id+"F16.imprint","IMPRINT",EDGE,{"derivedFrom":subQ3}),-1.0]])]});}
            var Q34;
            {var subQ1=sQuery(id+"F16.wireOp",EDGE,"E53.0.1.1");Q34=makeQuery(id+"F16.imprint","IMPRINT",FACE,{"disambiguationData":[TD([[makeQuery(id+"F16.imprint","IMPRINT",EDGE,{"derivedFrom":subQ1}),-1.0]])]});}
            var Q35;
            {var subQ1=sQuery(id+"F16.wireOp",EDGE,"E53.5.6.1");Q35=makeQuery(id+"F16.imprint","IMPRINT",FACE,{"disambiguationData":[TD([[makeQuery(id+"F16.imprint","IMPRINT",EDGE,{"derivedFrom":subQ1}),-1.0]])]});}
            var Q36;
            {var subQ1=sQuery(id+"F16.wireOp",EDGE,"E53.5.5.1");Q36=makeQuery(id+"F16.imprint","IMPRINT",FACE,{"disambiguationData":[TD([[makeQuery(id+"F16.imprint","IMPRINT",EDGE,{"derivedFrom":subQ1}),-1.0]])]});}
            var Q37;
            {var subQ3=sQuery(id+"F16.wireOp",EDGE,"E53.5.4.1");Q37=makeQuery(id+"F16.imprint","IMPRINT",FACE,{"disambiguationData":[TD([[makeQuery(id+"F16.imprint","IMPRINT",EDGE,{"derivedFrom":subQ3}),-1.0]])]});}
            var Q38;
            {var subQ0=sQuery(id+"F16.wireOp",EDGE,"E53.5.3.1");Q38=makeQuery(id+"F16.imprint","IMPRINT",FACE,{"disambiguationData":[TD([[makeQuery(id+"F16.imprint","IMPRINT",EDGE,{"derivedFrom":subQ0}),-1.0]])]});}
            var Q39;
            {var subQ1=sQuery(id+"F16.wireOp",EDGE,"E53.5.2.1");Q39=makeQuery(id+"F16.imprint","IMPRINT",FACE,{"disambiguationData":[TD([[makeQuery(id+"F16.imprint","IMPRINT",EDGE,{"derivedFrom":subQ1}),-1.0]])]});}
            var Q40;
            {var subQ1=sQuery(id+"F16.wireOp",EDGE,"E53.5.1.1");Q40=makeQuery(id+"F16.imprint","IMPRINT",FACE,{"disambiguationData":[TD([[makeQuery(id+"F16.imprint","IMPRINT",EDGE,{"derivedFrom":subQ1}),-1.0]])]});}
            var Q41;
            Q41=makeQuery(id+"F16.imprint","IMPRINT",FACE,{"disambiguationData":[TD([[makeQuery(id+"F16.imprint","IMPRINT",EDGE,{"derivedFrom":sQuery(id+"F16.wireOp",EDGE,"E53.5.0.0")}),1.0]])]});
            extrude(context, id + "F17", {"entities" : qUnion([Q0, Q1, Q2, Q3, Q4, Q5, Q6, Q7, Q8, Q9, Q10, Q11, Q12, Q13, Q14, Q15, Q16, Q17, Q18, Q19, Q20, Q21, Q22, Q23, Q24, Q25, Q26, Q27, Q28, Q29, Q30, Q31, Q32, Q33, Q34, Q35, Q36, Q37, Q38, Q39, Q40, Q41]), "operationType" : NewBodyOperationType.ADD, "depth" : 1 * mm, "hasDraft" : true, "draftAngle" : 45 * degree, "draftPullDirection" : true});
        }
        {
            var Q0;
            Q0=makeQuery(id+"F16.imprint","IMPRINT",FACE,{"disambiguationData":[TD([[makeQuery(id+"F16.imprint","IMPRINT",EDGE,{"derivedFrom":sQuery(id+"F16.wireOp",EDGE,"E47")}),1.0]])]});
            var Q1;
            Q1=makeQuery(id+"F16.imprint","IMPRINT",FACE,{"disambiguationData":[TD([[makeQuery(id+"F16.imprint","IMPRINT",EDGE,{"derivedFrom":sQuery(id+"F16.wireOp",EDGE,"E51.0.1.0")}),-1.0]])]});
            var Q2;
            {var subQ1=sQuery(id+"F16.wireOp",EDGE,"E51.0.2.0");Q2=makeQuery(id+"F16.imprint","IMPRINT",FACE,{"disambiguationData":[TD([[makeQuery(id+"F16.imprint","IMPRINT",EDGE,{"derivedFrom":subQ1}),-1.0]])]});}
            var Q3;
            {var subQ2=sQuery(id+"F16.wireOp",EDGE,"E51.0.3.0");Q3=makeQuery(id+"F16.imprint","IMPRINT",FACE,{"disambiguationData":[TD([[makeQuery(id+"F16.imprint","IMPRINT",EDGE,{"derivedFrom":subQ2}),-1.0]])]});}
            var Q4;
            {var subQ1=sQuery(id+"F16.wireOp",EDGE,"E51.0.4.0");Q4=makeQuery(id+"F16.imprint","IMPRINT",FACE,{"disambiguationData":[TD([[makeQuery(id+"F16.imprint","IMPRINT",EDGE,{"derivedFrom":subQ1}),-1.0]])]});}
            var Q5;
            {var subQ1=sQuery(id+"F16.wireOp",EDGE,"E51.0.5.0");Q5=makeQuery(id+"F16.imprint","IMPRINT",FACE,{"disambiguationData":[TD([[makeQuery(id+"F16.imprint","IMPRINT",EDGE,{"derivedFrom":subQ1}),-1.0]])]});}
            var Q6;
            {var subQ2=sQuery(id+"F16.wireOp",EDGE,"E51.0.6.0");Q6=makeQuery(id+"F16.imprint","IMPRINT",FACE,{"disambiguationData":[TD([[makeQuery(id+"F16.imprint","IMPRINT",EDGE,{"derivedFrom":subQ2}),-1.0]])]});}
            var Q7;
            {var subQ1=sQuery(id+"F16.wireOp",EDGE,"E51.0.7.0");Q7=makeQuery(id+"F16.imprint","IMPRINT",FACE,{"disambiguationData":[TD([[makeQuery(id+"F16.imprint","IMPRINT",EDGE,{"derivedFrom":subQ1}),-1.0]])]});}
            var Q8;
            Q8=makeQuery(id+"F16.imprint","IMPRINT",FACE,{"disambiguationData":[TD([[makeQuery(id+"F16.imprint","IMPRINT",EDGE,{"derivedFrom":sQuery(id+"F16.wireOp",EDGE,"E51.1.0.0")}),1.0]])]});
            var Q9;
            Q9=makeQuery(id+"F16.imprint","IMPRINT",FACE,{"disambiguationData":[TD([[makeQuery(id+"F16.imprint","IMPRINT",EDGE,{"derivedFrom":sQuery(id+"F16.wireOp",EDGE,"E51.1.1.0")}),-1.0]])]});
            var Q10;
            Q10=makeQuery(id+"F16.imprint","IMPRINT",FACE,{"disambiguationData":[TD([[makeQuery(id+"F16.imprint","IMPRINT",EDGE,{"derivedFrom":sQuery(id+"F16.wireOp",EDGE,"E51.2.1.0")}),-1.0]])]});
            var Q11;
            Q11=makeQuery(id+"F16.imprint","IMPRINT",FACE,{"disambiguationData":[TD([[makeQuery(id+"F16.imprint","IMPRINT",EDGE,{"derivedFrom":sQuery(id+"F16.wireOp",EDGE,"E51.2.0.0")}),1.0]])]});
            var Q12;
            Q12=makeQuery(id+"F16.imprint","IMPRINT",FACE,{"disambiguationData":[TD([[makeQuery(id+"F16.imprint","IMPRINT",EDGE,{"derivedFrom":sQuery(id+"F16.wireOp",EDGE,"E51.3.0.0")}),1.0]])]});
            var Q13;
            Q13=makeQuery(id+"F16.imprint","IMPRINT",FACE,{"disambiguationData":[TD([[makeQuery(id+"F16.imprint","IMPRINT",EDGE,{"derivedFrom":sQuery(id+"F16.wireOp",EDGE,"E51.3.1.0")}),-1.0]])]});
            var Q14;
            Q14=makeQuery(id+"F16.imprint","IMPRINT",FACE,{"disambiguationData":[TD([[makeQuery(id+"F16.imprint","IMPRINT",EDGE,{"derivedFrom":sQuery(id+"F16.wireOp",EDGE,"E51.4.0.0")}),1.0]])]});
            var Q15;
            Q15=makeQuery(id+"F16.imprint","IMPRINT",FACE,{"disambiguationData":[TD([[makeQuery(id+"F16.imprint","IMPRINT",EDGE,{"derivedFrom":sQuery(id+"F16.wireOp",EDGE,"E51.4.1.0")}),-1.0]])]});
            var Q16;
            Q16=makeQuery(id+"F16.imprint","IMPRINT",FACE,{"disambiguationData":[TD([[makeQuery(id+"F16.imprint","IMPRINT",EDGE,{"derivedFrom":sQuery(id+"F16.wireOp",EDGE,"E51.5.0.0")}),1.0]])]});
            var Q17;
            Q17=makeQuery(id+"F16.imprint","IMPRINT",FACE,{"disambiguationData":[TD([[makeQuery(id+"F16.imprint","IMPRINT",EDGE,{"derivedFrom":sQuery(id+"F16.wireOp",EDGE,"E51.5.1.0")}),-1.0]])]});
            var Q18;
            {var subQ2=sQuery(id+"F16.wireOp",EDGE,"E51.1.2.0");Q18=makeQuery(id+"F16.imprint","IMPRINT",FACE,{"disambiguationData":[TD([[makeQuery(id+"F16.imprint","IMPRINT",EDGE,{"derivedFrom":subQ2}),-1.0]])]});}
            var Q19;
            {var subQ2=sQuery(id+"F16.wireOp",EDGE,"E51.2.2.0");Q19=makeQuery(id+"F16.imprint","IMPRINT",FACE,{"disambiguationData":[TD([[makeQuery(id+"F16.imprint","IMPRINT",EDGE,{"derivedFrom":subQ2}),-1.0]])]});}
            var Q20;
            {var subQ1=sQuery(id+"F16.wireOp",EDGE,"E51.3.2.0");Q20=makeQuery(id+"F16.imprint","IMPRINT",FACE,{"disambiguationData":[TD([[makeQuery(id+"F16.imprint","IMPRINT",EDGE,{"derivedFrom":subQ1}),-1.0]])]});}
            var Q21;
            {var subQ2=sQuery(id+"F16.wireOp",EDGE,"E51.4.2.0");Q21=makeQuery(id+"F16.imprint","IMPRINT",FACE,{"disambiguationData":[TD([[makeQuery(id+"F16.imprint","IMPRINT",EDGE,{"derivedFrom":subQ2}),-1.0]])]});}
            var Q22;
            {var subQ2=sQuery(id+"F16.wireOp",EDGE,"E51.5.2.0");Q22=makeQuery(id+"F16.imprint","IMPRINT",FACE,{"disambiguationData":[TD([[makeQuery(id+"F16.imprint","IMPRINT",EDGE,{"derivedFrom":subQ2}),-1.0]])]});}
            var Q23;
            {var subQ0=sQuery(id+"F16.wireOp",EDGE,"E51.5.3.0");Q23=makeQuery(id+"F16.imprint","IMPRINT",FACE,{"disambiguationData":[TD([[makeQuery(id+"F16.imprint","IMPRINT",EDGE,{"derivedFrom":subQ0}),-1.0]])]});}
            var Q24;
            {var subQ2=sQuery(id+"F16.wireOp",EDGE,"E51.4.3.0");Q24=makeQuery(id+"F16.imprint","IMPRINT",FACE,{"disambiguationData":[TD([[makeQuery(id+"F16.imprint","IMPRINT",EDGE,{"derivedFrom":subQ2}),-1.0]])]});}
            var Q25;
            {var subQ2=sQuery(id+"F16.wireOp",EDGE,"E51.3.3.0");Q25=makeQuery(id+"F16.imprint","IMPRINT",FACE,{"disambiguationData":[TD([[makeQuery(id+"F16.imprint","IMPRINT",EDGE,{"derivedFrom":subQ2}),-1.0]])]});}
            var Q26;
            {var subQ1=sQuery(id+"F16.wireOp",EDGE,"E51.2.3.0");Q26=makeQuery(id+"F16.imprint","IMPRINT",FACE,{"disambiguationData":[TD([[makeQuery(id+"F16.imprint","IMPRINT",EDGE,{"derivedFrom":subQ1}),-1.0]])]});}
            var Q27;
            {var subQ1=sQuery(id+"F16.wireOp",EDGE,"E51.1.3.0");Q27=makeQuery(id+"F16.imprint","IMPRINT",FACE,{"disambiguationData":[TD([[makeQuery(id+"F16.imprint","IMPRINT",EDGE,{"derivedFrom":subQ1}),-1.0]])]});}
            var Q28;
            {var subQ2=sQuery(id+"F16.wireOp",EDGE,"E51.1.4.0");Q28=makeQuery(id+"F16.imprint","IMPRINT",FACE,{"disambiguationData":[TD([[makeQuery(id+"F16.imprint","IMPRINT",EDGE,{"derivedFrom":subQ2}),-1.0]])]});}
            var Q29;
            {var subQ1=sQuery(id+"F16.wireOp",EDGE,"E51.2.4.0");Q29=makeQuery(id+"F16.imprint","IMPRINT",FACE,{"disambiguationData":[TD([[makeQuery(id+"F16.imprint","IMPRINT",EDGE,{"derivedFrom":subQ1}),-1.0]])]});}
            var Q30;
            {var subQ2=sQuery(id+"F16.wireOp",EDGE,"E51.3.4.0");Q30=makeQuery(id+"F16.imprint","IMPRINT",FACE,{"disambiguationData":[TD([[makeQuery(id+"F16.imprint","IMPRINT",EDGE,{"derivedFrom":subQ2}),-1.0]])]});}
            var Q31;
            {var subQ2=sQuery(id+"F16.wireOp",EDGE,"E51.4.4.0");Q31=makeQuery(id+"F16.imprint","IMPRINT",FACE,{"disambiguationData":[TD([[makeQuery(id+"F16.imprint","IMPRINT",EDGE,{"derivedFrom":subQ2}),-1.0]])]});}
            var Q32;
            {var subQ2=sQuery(id+"F16.wireOp",EDGE,"E51.5.4.0");Q32=makeQuery(id+"F16.imprint","IMPRINT",FACE,{"disambiguationData":[TD([[makeQuery(id+"F16.imprint","IMPRINT",EDGE,{"derivedFrom":subQ2}),-1.0]])]});}
            var Q33;
            {var subQ2=sQuery(id+"F16.wireOp",EDGE,"E51.1.5.0");Q33=makeQuery(id+"F16.imprint","IMPRINT",FACE,{"disambiguationData":[TD([[makeQuery(id+"F16.imprint","IMPRINT",EDGE,{"derivedFrom":subQ2}),-1.0]])]});}
            var Q34;
            {var subQ2=sQuery(id+"F16.wireOp",EDGE,"E51.2.5.0");Q34=makeQuery(id+"F16.imprint","IMPRINT",FACE,{"disambiguationData":[TD([[makeQuery(id+"F16.imprint","IMPRINT",EDGE,{"derivedFrom":subQ2}),-1.0]])]});}
            var Q35;
            {var subQ2=sQuery(id+"F16.wireOp",EDGE,"E51.3.5.0");Q35=makeQuery(id+"F16.imprint","IMPRINT",FACE,{"disambiguationData":[TD([[makeQuery(id+"F16.imprint","IMPRINT",EDGE,{"derivedFrom":subQ2}),-1.0]])]});}
            var Q36;
            {var subQ2=sQuery(id+"F16.wireOp",EDGE,"E51.4.5.0");Q36=makeQuery(id+"F16.imprint","IMPRINT",FACE,{"disambiguationData":[TD([[makeQuery(id+"F16.imprint","IMPRINT",EDGE,{"derivedFrom":subQ2}),-1.0]])]});}
            var Q37;
            {var subQ1=sQuery(id+"F16.wireOp",EDGE,"E51.5.5.0");Q37=makeQuery(id+"F16.imprint","IMPRINT",FACE,{"disambiguationData":[TD([[makeQuery(id+"F16.imprint","IMPRINT",EDGE,{"derivedFrom":subQ1}),-1.0]])]});}
            var Q38;
            {var subQ2=sQuery(id+"F16.wireOp",EDGE,"E51.1.6.0");Q38=makeQuery(id+"F16.imprint","IMPRINT",FACE,{"disambiguationData":[TD([[makeQuery(id+"F16.imprint","IMPRINT",EDGE,{"derivedFrom":subQ2}),-1.0]])]});}
            var Q39;
            {var subQ2=sQuery(id+"F16.wireOp",EDGE,"E51.2.6.0");Q39=makeQuery(id+"F16.imprint","IMPRINT",FACE,{"disambiguationData":[TD([[makeQuery(id+"F16.imprint","IMPRINT",EDGE,{"derivedFrom":subQ2}),-1.0]])]});}
            var Q40;
            {var subQ2=sQuery(id+"F16.wireOp",EDGE,"E51.3.6.0");Q40=makeQuery(id+"F16.imprint","IMPRINT",FACE,{"disambiguationData":[TD([[makeQuery(id+"F16.imprint","IMPRINT",EDGE,{"derivedFrom":subQ2}),-1.0]])]});}
            var Q41;
            {var subQ2=sQuery(id+"F16.wireOp",EDGE,"E51.4.6.0");Q41=makeQuery(id+"F16.imprint","IMPRINT",FACE,{"disambiguationData":[TD([[makeQuery(id+"F16.imprint","IMPRINT",EDGE,{"derivedFrom":subQ2}),-1.0]])]});}
            var Q42;
            {var subQ3=sQuery(id+"F16.wireOp",EDGE,"E51.5.6.0");Q42=makeQuery(id+"F16.imprint","IMPRINT",FACE,{"disambiguationData":[TD([[makeQuery(id+"F16.imprint","IMPRINT",EDGE,{"derivedFrom":subQ3}),-1.0]])]});}
            var Q43;
            {var subQ2=sQuery(id+"F16.wireOp",EDGE,"E51.5.7.0");Q43=makeQuery(id+"F16.imprint","IMPRINT",FACE,{"disambiguationData":[TD([[makeQuery(id+"F16.imprint","IMPRINT",EDGE,{"derivedFrom":subQ2}),-1.0]])]});}
            var Q44;
            {var subQ2=sQuery(id+"F16.wireOp",EDGE,"E51.4.7.0");Q44=makeQuery(id+"F16.imprint","IMPRINT",FACE,{"disambiguationData":[TD([[makeQuery(id+"F16.imprint","IMPRINT",EDGE,{"derivedFrom":subQ2}),-1.0]])]});}
            var Q45;
            {var subQ2=sQuery(id+"F16.wireOp",EDGE,"E51.3.7.0");Q45=makeQuery(id+"F16.imprint","IMPRINT",FACE,{"disambiguationData":[TD([[makeQuery(id+"F16.imprint","IMPRINT",EDGE,{"derivedFrom":subQ2}),-1.0]])]});}
            var Q46;
            {var subQ2=sQuery(id+"F16.wireOp",EDGE,"E51.2.7.0");Q46=makeQuery(id+"F16.imprint","IMPRINT",FACE,{"disambiguationData":[TD([[makeQuery(id+"F16.imprint","IMPRINT",EDGE,{"derivedFrom":subQ2}),-1.0]])]});}
            var Q47;
            {var subQ1=sQuery(id+"F16.wireOp",EDGE,"E51.1.7.0");Q47=makeQuery(id+"F16.imprint","IMPRINT",FACE,{"disambiguationData":[TD([[makeQuery(id+"F16.imprint","IMPRINT",EDGE,{"derivedFrom":subQ1}),-1.0]])]});}
            extrude(context, id + "F18", {"entities" : qUnion([Q0, Q1, Q2, Q3, Q4, Q5, Q6, Q7, Q8, Q9, Q10, Q11, Q12, Q13, Q14, Q15, Q16, Q17, Q18, Q19, Q20, Q21, Q22, Q23, Q24, Q25, Q26, Q27, Q28, Q29, Q30, Q31, Q32, Q33, Q34, Q35, Q36, Q37, Q38, Q39, Q40, Q41, Q42, Q43, Q44, Q45, Q46, Q47]), "operationType" : NewBodyOperationType.ADD, "depth" : 1 * mm, "hasDraft" : true, "draftAngle" : 45 * degree, "draftPullDirection" : true});
        }
    });
